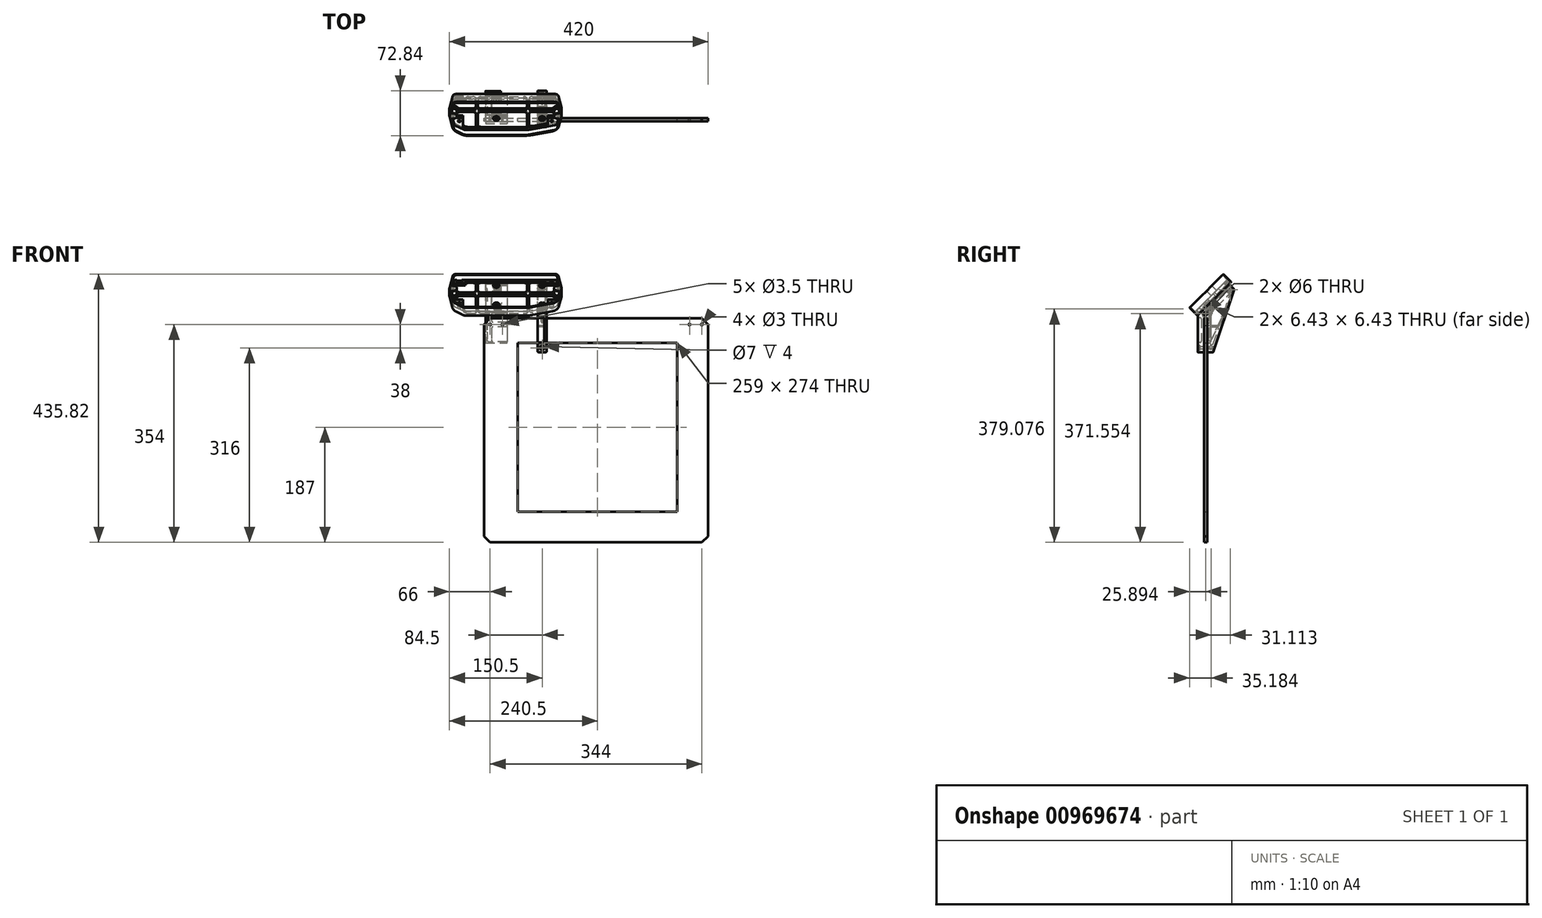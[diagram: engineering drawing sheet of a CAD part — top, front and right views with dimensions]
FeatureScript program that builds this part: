
annotation { "Feature Type Name" : "Feature", "Feature Type Description" : "" }
export const myFeature = defineFeature(function(context is Context, id is Id, definition is map)
    precondition{}
    {
        {
            var Q0;
            Q0=qCreatedBy(makeId("Front.planeOp"),FACE);
            var sketch = newSketch(context, id + "F0", { "sketchPlane" : qUnion([Q0])});
            skLineSegment(sketch, "E0.bottom", {"start": v(-182, 182) * mm, "end": v(182, 182) * mm});
            skLineSegment(sketch, "E0.top", {"start": v(-182, -182) * mm, "end": v(182, -182) * mm});
            skLineSegment(sketch, "E0.left", {"start": v(-182, 182) * mm, "end": v(-182, -182) * mm});
            skLineSegment(sketch, "E0.right", {"start": v(182, 182) * mm, "end": v(182, -182) * mm});
            skLineSegment(sketch, "E1", {"start": v(-182, 0) * mm, "end": v(0, 0) * mm, "construction": true});
            skLineSegment(sketch, "E2", {"start": v(0, 0) * mm, "end": v(0, 182) * mm, "construction": true});
            skLineSegment(sketch, "E3.bottom", {"start": v(-127, 142) * mm, "end": v(132, 142) * mm});
            skLineSegment(sketch, "E3.top", {"start": v(-127, -132) * mm, "end": v(132, -132) * mm});
            skLineSegment(sketch, "E3.left", {"start": v(-127, 142) * mm, "end": v(-127, -132) * mm});
            skLineSegment(sketch, "E3.right", {"start": v(132, 142) * mm, "end": v(132, -132) * mm});
            skCircle(sketch, "E4", {"center": v(172, 172) * mm, "radius": 1.5 * mm});
            skCircle(sketch, "E5", {"center": v(152, 172) * mm, "radius": 1.5 * mm});
            skCircle(sketch, "E6", {"center": v(-152, 172) * mm, "radius": 1.5 * mm});
            skCircle(sketch, "E7", {"center": v(-172, 172) * mm, "radius": 1.5 * mm});
            skSolve(sketch);
        }
        {
            var Q0;
            Q0=makeQuery(id+"F0.imprint","IMPRINT",FACE,{"disambiguationData":[TD([[makeQuery(id+"F0.imprint","IMPRINT",EDGE,{"derivedFrom":sQuery(id+"F0.wireOp",EDGE,"E0.bottom")}),-1.0]])]});
            extrude(context, id + "F1", {"entities" : qUnion([Q0]), "depth" : 5 * mm, "offsetDistance" : 25 * mm});
        }
        {
            var Q0;
            Q0=makeQuery(id+"F1.opExtrude","SWEPT_EDGE",EDGE,{"disambiguationData":[OSD([sQuery(id+"F0.wireOp",EDGE,"E0.bottom"),sQuery(id+"F0.wireOp",EDGE,"E0.left")])]});
            var Q1;
            Q1=makeQuery(id+"F1.opExtrude","SWEPT_EDGE",EDGE,{"disambiguationData":[OSD([sQuery(id+"F0.wireOp",EDGE,"E0.top"),sQuery(id+"F0.wireOp",EDGE,"E0.left")])]});
            var Q2;
            Q2=makeQuery(id+"F1.opExtrude","SWEPT_EDGE",EDGE,{"disambiguationData":[OSD([sQuery(id+"F0.wireOp",EDGE,"E0.top"),sQuery(id+"F0.wireOp",EDGE,"E0.right")])]});
            var Q3;
            Q3=makeQuery(id+"F1.opExtrude","SWEPT_EDGE",EDGE,{"disambiguationData":[OSD([sQuery(id+"F0.wireOp",EDGE,"E0.bottom"),sQuery(id+"F0.wireOp",EDGE,"E0.right")])]});
            chamfer(context, id + "F2", {"entities" : qUnion([Q0, Q1, Q2, Q3]), "width" : 10 * mm, "tangentPropagation" : true});
        }
        {
            var Q0;
            Q0=qCreatedBy(makeId("Right.planeOp"),FACE);
            cPlane(context, id + "F3", {"entities" : qUnion([Q0]), "cplaneType" : CPlaneType.OFFSET, "offset" : 80 * mm, "oppositeDirection" : true, "width" : 150 * mm, "height" : 150 * mm});
        }
        {
            var Q0;
            Q0=qCreatedBy(id+"F3.planeOp",FACE);
            var sketch = newSketch(context, id + "F4", { "sketchPlane" : qUnion([Q0])});
            skLineSegment(sketch, "E8", {"start": v(-5, 127) * mm, "end": v(-15, 127) * mm});
            skLineSegment(sketch, "E9", {"start": v(-15, 127) * mm, "end": v(-15, 187) * mm});
            skLineSegment(sketch, "E10", {"start": v(-15, 187) * mm, "end": v(35.91, 237.91) * mm});
            skLineSegment(sketch, "E11", {"start": v(35.91, 237.91) * mm, "end": v(44.4, 229.43) * mm});
            skLineSegment(sketch, "E12", {"start": v(44.4, 229.43) * mm, "end": v(10, 127) * mm});
            skLineSegment(sketch, "E13", {"start": v(10, 127) * mm, "end": v(0, 127) * mm});
            skLineSegment(sketch, "E14", {"start": v(0, 127) * mm, "end": v(0, 182) * mm});
            skLineSegment(sketch, "E15", {"start": v(0, 182) * mm, "end": v(-5, 182) * mm});
            skLineSegment(sketch, "E16", {"start": v(-5, 182) * mm, "end": v(-5, 127) * mm});
            skSolve(sketch);
        }
        {
            var Q0;
            Q0=makeQuery(id+"F4.imprint","IMPRINT",FACE,{"disambiguationData":[TD([[makeQuery(id+"F4.imprint","IMPRINT",EDGE,{"derivedFrom":sQuery(id+"F4.wireOp",EDGE,"E8")}),-1.0]])]});
            extrude(context, id + "F5", {"entities" : qUnion([Q0]), "oppositeDirection" : true, "depth" : 15 * mm, "offsetDistance" : 25 * mm});
        }
        {
            var Q0;
            Q0=makeQuery(id+"F5.opExtrude","SWEPT_FACE",FACE,{"disambiguationData":[OSD([sQuery(id+"F4.wireOp",EDGE,"E10")])]});
            var sketch = newSketch(context, id + "F6", { "sketchPlane" : qUnion([Q0])});
            skLineSegment(sketch, "E17.bottom", {"start": v(-232, 198.12) * mm, "end": v(-62, 198.12) * mm});
            skLineSegment(sketch, "E17.top", {"start": v(-232, 133.12) * mm, "end": v(-62, 133.12) * mm, "construction": true});
            skLineSegment(sketch, "E17.left", {"start": v(-232, 198.12) * mm, "end": v(-232, 133.12) * mm, "construction": true});
            skLineSegment(sketch, "E17.right", {"start": v(-62, 198.12) * mm, "end": v(-62, 133.12) * mm, "construction": true});
            skPoint(sketch, "E18.visualSharp", {"position": v(-232, 198.12) * mm});
            skPoint(sketch, "E19.visualSharp", {"position": v(-62, 133.12) * mm});
            skPoint(sketch, "E20.visualSharp", {"position": v(-232, 133.12) * mm});
            skLineSegment(sketch, "E21", {"start": v(-232, 133.12) * mm, "end": v(-214, 120.62) * mm});
            skLineSegment(sketch, "E22", {"start": v(-214, 120.62) * mm, "end": v(-110, 120.62) * mm});
            skLineSegment(sketch, "E23", {"start": v(-110, 120.62) * mm, "end": v(-62, 133.12) * mm});
            skLineSegment(sketch, "E24", {"start": v(-232, 133.12) * mm, "end": v(-237.9, 164.51) * mm});
            skLineSegment(sketch, "E25", {"start": v(-237.9, 166.73) * mm, "end": v(-232, 198.12) * mm});
            skLineSegment(sketch, "E26", {"start": v(-62, 198.12) * mm, "end": v(-56.1, 166.73) * mm});
            skLineSegment(sketch, "E27", {"start": v(-56.1, 164.51) * mm, "end": v(-62, 133.12) * mm});
            skPoint(sketch, "E28.visualSharp", {"position": v(-238.1, 165.62) * mm});
            skArc(sketch, "E28.filletArc", {"start": v(-237.9, 166.73) * mm, "mid": v(-238, 165.62) * mm, "end": v(-237.9, 164.51) * mm});
            skPoint(sketch, "E29.visualSharp", {"position": v(-55.9, 165.62) * mm});
            skArc(sketch, "E29.filletArc", {"start": v(-56.1, 164.51) * mm, "mid": v(-56, 165.62) * mm, "end": v(-56.1, 166.73) * mm});
            skLineSegment(sketch, "E30", {"start": v(-147, 198.12) * mm, "end": v(-147, 134.38) * mm, "construction": true});
            skSolve(sketch);
        }
        {
            var Q0;
            Q0 = qSketchRegion(id + "F6", true);
            extrude(context, id + "F7", {"entities" : qUnion([Q0]), "depth" : 18 * mm, "offsetDistance" : 25 * mm});
        }
        {
            var Q0;
            Q0=makeQuery(id+"F7.opExtrude","SWEPT_EDGE",EDGE,{"disambiguationData":[OSD([sQuery(id+"F6.wireOp",EDGE,"E21"),sQuery(id+"F6.wireOp",EDGE,"E24")])]});
            var Q1;
            Q1=makeQuery(id+"F7.opExtrude","SWEPT_EDGE",EDGE,{"disambiguationData":[OSD([sQuery(id+"F6.wireOp",EDGE,"E21"),sQuery(id+"F6.wireOp",EDGE,"E22")])]});
            var Q2;
            Q2=makeQuery(id+"F7.opExtrude","SWEPT_EDGE",EDGE,{"disambiguationData":[OSD([sQuery(id+"F6.wireOp",EDGE,"E23"),sQuery(id+"F6.wireOp",EDGE,"E27")])]});
            fillet(context, id + "F8", {"entities" : qUnion([Q0, Q1, Q2]), "radius" : 15 * mm, "tangentPropagation" : true, "allowEdgeOverflow" : false});
        }
        {
            var Q0;
            Q0=makeQuery(id+"F7.opExtrude","SWEPT_EDGE",EDGE,{"disambiguationData":[OSD([sQuery(id+"F6.wireOp",EDGE,"E22"),sQuery(id+"F6.wireOp",EDGE,"E23")])]});
            fillet(context, id + "F9", {"entities" : qUnion([Q0]), "radius" : 60 * mm, "tangentPropagation" : true, "allowEdgeOverflow" : false});
        }
        {
            var Q0;
            Q0=makeQuery(id+"F7.opExtrude","SWEPT_EDGE",EDGE,{"disambiguationData":[OSD([sQuery(id+"F6.wireOp",EDGE,"E17.bottom"),sQuery(id+"F6.wireOp",EDGE,"E25")])]});
            var Q1;
            Q1=makeQuery(id+"F7.opExtrude","SWEPT_EDGE",EDGE,{"disambiguationData":[OSD([sQuery(id+"F6.wireOp",EDGE,"E17.bottom"),sQuery(id+"F6.wireOp",EDGE,"E26")])]});
            fillet(context, id + "F10", {"entities" : qUnion([Q0, Q1]), "radius" : 5 * mm, "tangentPropagation" : true, "allowEdgeOverflow" : false});
        }
        {
            var Q0;
            Q0=makeQuery(id+"F5.opExtrude","SWEPT_FACE",FACE,{"disambiguationData":[OSD([sQuery(id+"F4.wireOp",EDGE,"E9")])]});
            var sketch = newSketch(context, id + "F11", { "sketchPlane" : qUnion([Q0])});
            skPoint(sketch, "E31", {"position": v(-87.5, 134) * mm});
            skPoint(sketch, "E31.positionSnap0", {"position": v(-87.5, 127) * mm});
            skSolve(sketch);
        }
        {
            var Q0;
            Q0=sQuery(id+"F11.wireOp",VERTEX,"E31");
            var Q1;
            Q1=makeQuery(id+"F5.opExtrude","SWEPT_BODY",BODY,{"disambiguationData":[OSD([sQuery(id+"F4.wireOp",EDGE,"E8"),sQuery(id+"F4.wireOp",EDGE,"E9"),sQuery(id+"F4.wireOp",EDGE,"E10"),sQuery(id+"F4.wireOp",EDGE,"E11"),sQuery(id+"F4.wireOp",EDGE,"E12"),sQuery(id+"F4.wireOp",EDGE,"E13"),sQuery(id+"F4.wireOp",EDGE,"E14"),sQuery(id+"F4.wireOp",EDGE,"E15"),sQuery(id+"F4.wireOp",EDGE,"E16")])]});
            hole(context, id + "F12", {"style" : HoleStyle.C_BORE, "endStyle" : HoleEndStyle.THROUGH, "holeDiameter" : 3.5 * mm, "cBoreDiameter" : 7 * mm, "cBoreDepth" : 4 * mm, "majorDiameter" : 5 * mm, "isTappedThrough" : true, "tappedDepth" : 12 * mm, "tapClearance" : 3, "locations" : qUnion([Q0]), "scope" : qUnion([Q1])});
        }
        {
            var Q0;
            Q0=makeQuery(id+"F7.opExtrude","CAP_FACE",FACE,{"disambiguationData":[OSD([sQuery(id+"F6.wireOp",EDGE,"E17.bottom"),sQuery(id+"F6.wireOp",EDGE,"E17.top"),sQuery(id+"F6.wireOp",EDGE,"E17.left"),sQuery(id+"F6.wireOp",EDGE,"E17.right")])],"isStart":true});
            var sketch = newSketch(context, id + "F13", { "sketchPlane" : qUnion([Q0])});
            skLineSegment(sketch, "E32.bottom", {"start": v(67, 196.17) * mm, "end": v(77, 196.17) * mm});
            skLineSegment(sketch, "E32.top", {"start": v(67, 190.07) * mm, "end": v(77, 190.07) * mm});
            skLineSegment(sketch, "E32.left", {"start": v(67, 196.17) * mm, "end": v(67, 190.07) * mm, "construction": true});
            skLineSegment(sketch, "E32.right", {"start": v(77, 196.17) * mm, "end": v(77, 190.07) * mm, "construction": true});
            skLineSegment(sketch, "E33.bottom", {"start": v(68.95, 138.12) * mm, "end": v(75.05, 138.12) * mm, "construction": true});
            skLineSegment(sketch, "E33.top", {"start": v(68.95, 148.12) * mm, "end": v(75.05, 148.12) * mm, "construction": true});
            skLineSegment(sketch, "E33.right", {"start": v(75.05, 138.12) * mm, "end": v(75.05, 148.12) * mm});
            skLineSegment(sketch, "E34.bottom", {"start": v(218.95, 148.12) * mm, "end": v(225.05, 148.12) * mm, "construction": true});
            skLineSegment(sketch, "E34.top", {"start": v(218.95, 138.12) * mm, "end": v(225.05, 138.12) * mm, "construction": true});
            skLineSegment(sketch, "E34.left", {"start": v(218.95, 148.12) * mm, "end": v(218.95, 138.12) * mm});
            skLineSegment(sketch, "E34.right", {"start": v(225.05, 148.12) * mm, "end": v(225.05, 138.12) * mm});
            skPoint(sketch, "E35.firstSnap0", {"position": v(72, 196.17) * mm});
            skLineSegment(sketch, "E35.bottom", {"start": v(72, 193.12) * mm, "end": v(222, 193.12) * mm, "construction": true});
            skLineSegment(sketch, "E35.top", {"start": v(72, 143.12) * mm, "end": v(222, 143.12) * mm, "construction": true});
            skLineSegment(sketch, "E35.left", {"start": v(72, 193.12) * mm, "end": v(72, 143.12) * mm, "construction": true});
            skLineSegment(sketch, "E35.right", {"start": v(222, 193.12) * mm, "end": v(222, 143.12) * mm, "construction": true});
            skLineSegment(sketch, "E36.bottom", {"start": v(227, 196.17) * mm, "end": v(217, 196.17) * mm});
            skLineSegment(sketch, "E36.top", {"start": v(227, 190.07) * mm, "end": v(217, 190.07) * mm});
            skLineSegment(sketch, "E36.left", {"start": v(227, 196.17) * mm, "end": v(227, 190.07) * mm, "construction": true});
            skLineSegment(sketch, "E36.right", {"start": v(217, 196.17) * mm, "end": v(217, 190.07) * mm, "construction": true});
            skLineSegment(sketch, "E37", {"start": v(68.95, 138.12) * mm, "end": v(68.95, 148.12) * mm});
            skLineSegment(sketch, "E38", {"start": v(67, 196.17) * mm, "end": v(65.24, 193.12) * mm});
            skLineSegment(sketch, "E39", {"start": v(65.24, 193.12) * mm, "end": v(67, 190.07) * mm});
            skLineSegment(sketch, "E40", {"start": v(77, 190.07) * mm, "end": v(78.76, 193.12) * mm});
            skLineSegment(sketch, "E41", {"start": v(78.76, 193.12) * mm, "end": v(77, 196.17) * mm});
            skLineSegment(sketch, "E42", {"start": v(68.95, 148.12) * mm, "end": v(72, 149.88) * mm});
            skLineSegment(sketch, "E43", {"start": v(72, 149.88) * mm, "end": v(75.05, 148.12) * mm});
            skLineSegment(sketch, "E44", {"start": v(72, 136.36) * mm, "end": v(75.05, 138.12) * mm});
            skLineSegment(sketch, "E45", {"start": v(68.95, 138.12) * mm, "end": v(72, 136.36) * mm});
            skLineSegment(sketch, "E46", {"start": v(218.95, 148.12) * mm, "end": v(222, 149.88) * mm});
            skLineSegment(sketch, "E47", {"start": v(222, 149.88) * mm, "end": v(225.05, 148.12) * mm});
            skLineSegment(sketch, "E48", {"start": v(225.05, 138.12) * mm, "end": v(222, 136.36) * mm});
            skLineSegment(sketch, "E49", {"start": v(222, 136.36) * mm, "end": v(218.95, 138.12) * mm});
            skLineSegment(sketch, "E50", {"start": v(227, 196.17) * mm, "end": v(228.76, 193.12) * mm});
            skLineSegment(sketch, "E51", {"start": v(228.76, 193.12) * mm, "end": v(227, 190.07) * mm});
            skLineSegment(sketch, "E52", {"start": v(217, 190.07) * mm, "end": v(215.24, 193.12) * mm});
            skLineSegment(sketch, "E53", {"start": v(215.24, 193.12) * mm, "end": v(217, 196.17) * mm});
            skSolve(sketch);
        }
        {
            var Q0;
            Q0 = qSketchRegion(id + "F13", true);
            extrude(context, id + "F14", {"entities" : qUnion([Q0]), "operationType" : NewBodyOperationType.REMOVE, "oppositeDirection" : true, "depth" : 4 * mm, "offsetDistance" : 25 * mm});
        }
        {
            var Q0;
            Q0=sQuery(id+"F13.wireOp",VERTEX,"E35.bottom.start");
            var Q1;
            Q1=sQuery(id+"F13.wireOp",VERTEX,"E35.bottom.end");
            var Q2;
            Q2=sQuery(id+"F13.wireOp",VERTEX,"E35.top.end");
            var Q3;
            Q3=sQuery(id+"F13.wireOp",VERTEX,"E35.top.start");
            var Q4;
            Q4=makeQuery(id+"F7.opExtrude","SWEPT_BODY",BODY,{"disambiguationData":[OSD([sQuery(id+"F6.wireOp",EDGE,"E17.bottom"),sQuery(id+"F6.wireOp",EDGE,"E17.top"),sQuery(id+"F6.wireOp",EDGE,"E17.left"),sQuery(id+"F6.wireOp",EDGE,"E17.right")])]});
            hole(context, id + "F15", {"style" : HoleStyle.SIMPLE, "endStyle" : HoleEndStyle.THROUGH, "standardTappedOrClearance" : lookupTablePath({ "fit" : "Normal", "standard" : "ISO", "size" : "M3", "type" : "Clearance" }), "standardBlindInLast" : lookupTablePath({ "fit" : "Normal", "standard" : "ISO", "engagement" : "75%", "pitch" : "0.5 mm", "size" : "M3", "type" : "Clearance & tapped" }), "holeDiameter" : 3.4 * mm, "majorDiameter" : 5 * mm, "isTappedThrough" : true, "tappedDepth" : 12 * mm, "tapClearance" : 3, "locations" : qUnion([Q0, Q1, Q2, Q3]), "scope" : qUnion([Q4])});
        }
        {
            var Q0;
            Q0=makeQuery(id+"F7.opExtrude","CAP_FACE",FACE,{"disambiguationData":[OSD([sQuery(id+"F6.wireOp",EDGE,"E17.bottom"),sQuery(id+"F6.wireOp",EDGE,"E21"),sQuery(id+"F6.wireOp",EDGE,"E22"),sQuery(id+"F6.wireOp",EDGE,"E23"),sQuery(id+"F6.wireOp",EDGE,"E24"),sQuery(id+"F6.wireOp",EDGE,"E25"),sQuery(id+"F6.wireOp",EDGE,"E26"),sQuery(id+"F6.wireOp",EDGE,"E27"),sQuery(id+"F6.wireOp",EDGE,"E28.filletArc"),sQuery(id+"F6.wireOp",EDGE,"E29.filletArc")])],"isStart":false});
            var sketch = newSketch(context, id + "F16", { "sketchPlane" : qUnion([Q0])});
            skArc(sketch, "E54", {"start": v(-232.4, 171.6) * mm, "mid": v(-226, 165.62) * mm, "end": v(-232.4, 159.64) * mm});
            skLineSegment(sketch, "E55", {"start": v(-234.5, 173.97) * mm, "end": v(-231.1, 192.05) * mm});
            skLineSegment(sketch, "E56", {"start": v(-226.2, 196.12) * mm, "end": v(-67.8, 196.12) * mm});
            skLineSegment(sketch, "E57", {"start": v(-59.5, 157.27) * mm, "end": v(-63.15, 137.85) * mm});
            skLineSegment(sketch, "E58", {"start": v(-66.8, 133.94) * mm, "end": v(-109.64, 122.78) * mm});
            skLineSegment(sketch, "E59", {"start": v(-110.9, 122.62) * mm, "end": v(-211.8, 122.62) * mm});
            skLineSegment(sketch, "E60", {"start": v(-214.66, 123.52) * mm, "end": v(-228.5, 133.13) * mm});
            skLineSegment(sketch, "E61", {"start": v(-230.56, 136.31) * mm, "end": v(-234.5, 157.27) * mm});
            skArc(sketch, "E62", {"start": v(-61.6, 171.6) * mm, "mid": v(-68, 165.62) * mm, "end": v(-61.6, 159.64) * mm});
            skLineSegment(sketch, "E63", {"start": v(-62.9, 192.05) * mm, "end": v(-59.5, 173.97) * mm});
            skPoint(sketch, "E64.visualSharp", {"position": v(-235.1, 170.76) * mm});
            skArc(sketch, "E64.filletArc", {"start": v(-234.5, 173.97) * mm, "mid": v(-234.03, 172.28) * mm, "end": v(-232.4, 171.6) * mm});
            skPoint(sketch, "E65.visualSharp", {"position": v(-235.1, 160.49) * mm});
            skArc(sketch, "E65.filletArc", {"start": v(-232.4, 159.64) * mm, "mid": v(-234.03, 158.97) * mm, "end": v(-234.5, 157.27) * mm});
            skPoint(sketch, "E66.visualSharp", {"position": v(-58.9, 170.76) * mm});
            skArc(sketch, "E66.filletArc", {"start": v(-61.6, 171.6) * mm, "mid": v(-59.97, 172.28) * mm, "end": v(-59.5, 173.97) * mm});
            skPoint(sketch, "E67.visualSharp", {"position": v(-58.9, 160.49) * mm});
            skArc(sketch, "E67.filletArc", {"start": v(-59.5, 157.27) * mm, "mid": v(-59.97, 158.97) * mm, "end": v(-61.6, 159.64) * mm});
            skPoint(sketch, "E68.visualSharp", {"position": v(-63.66, 196.12) * mm});
            skArc(sketch, "E68.filletArc", {"start": v(-62.9, 192.05) * mm, "mid": v(-64.61, 194.97) * mm, "end": v(-67.8, 196.12) * mm});
            skPoint(sketch, "E69.visualSharp", {"position": v(-63.73, 134.74) * mm});
            skArc(sketch, "E69.filletArc", {"start": v(-66.8, 133.94) * mm, "mid": v(-64.4, 135.37) * mm, "end": v(-63.15, 137.85) * mm});
            skPoint(sketch, "E70.visualSharp", {"position": v(-110.26, 122.62) * mm});
            skArc(sketch, "E70.filletArc", {"start": v(-110.9, 122.62) * mm, "mid": v(-110.26, 122.66) * mm, "end": v(-109.64, 122.78) * mm});
            skPoint(sketch, "E71.visualSharp", {"position": v(-213.37, 122.62) * mm});
            skArc(sketch, "E71.filletArc", {"start": v(-214.66, 123.52) * mm, "mid": v(-213.3, 122.85) * mm, "end": v(-211.8, 122.62) * mm});
            skPoint(sketch, "E72.visualSharp", {"position": v(-230.19, 134.3) * mm});
            skArc(sketch, "E72.filletArc", {"start": v(-230.56, 136.31) * mm, "mid": v(-229.85, 134.52) * mm, "end": v(-228.5, 133.13) * mm});
            skPoint(sketch, "E73.visualSharp", {"position": v(-230.34, 196.12) * mm});
            skArc(sketch, "E73.filletArc", {"start": v(-226.2, 196.12) * mm, "mid": v(-229.39, 194.97) * mm, "end": v(-231.1, 192.05) * mm});
            skSolve(sketch);
        }
        {
            var Q0;
            Q0 = qSketchRegion(id + "F16", true);
            extrude(context, id + "F17", {"entities" : qUnion([Q0]), "operationType" : NewBodyOperationType.REMOVE, "oppositeDirection" : true, "depth" : 11 * mm, "offsetDistance" : 25 * mm});
        }
        {
            var Q0;
            Q0=qCreatedBy(id+"F3.planeOp",FACE);
            cPlane(context, id + "F18", {"entities" : qUnion([Q0]), "cplaneType" : CPlaneType.OFFSET, "offset" : (65 + 17) * mm, "oppositeDirection" : true, "width" : 150 * mm, "height" : 150 * mm});
        }
        {
            var Q0;
            Q0=qCreatedBy(id+"F18.planeOp",FACE);
            var sketch = newSketch(context, id + "F19", { "sketchPlane" : qUnion([Q0])});
            skLineSegment(sketch, "E74", {"start": v(35.91, 237.91) * mm, "end": v(-9, 193) * mm});
            skLineSegment(sketch, "E75", {"start": v(0, 182) * mm, "end": v(0, 142) * mm});
            skLineSegment(sketch, "E76", {"start": v(0, 142) * mm, "end": v(5, 142) * mm});
            skLineSegment(sketch, "E77", {"start": v(5, 142) * mm, "end": v(44.4, 229.43) * mm});
            skLineSegment(sketch, "E78", {"start": v(44.4, 229.43) * mm, "end": v(35.91, 237.91) * mm});
            skLineSegment(sketch, "E79", {"start": v(0, 182) * mm, "end": v(-5, 182) * mm});
            skLineSegment(sketch, "E80", {"start": v(-5, 182) * mm, "end": v(-9, 193) * mm});
            skSolve(sketch);
        }
        {
            var Q0;
            Q0=makeQuery(id+"F19.imprint","IMPRINT",FACE,{"disambiguationData":[TD([[makeQuery(id+"F19.imprint","IMPRINT",EDGE,{"derivedFrom":sQuery(id+"F19.wireOp",EDGE,"E74")}),1.0]])]});
            extrude(context, id + "F20", {"entities" : qUnion([Q0]), "endBound" : BoundingType.SYMMETRIC, "oppositeDirection" : true, "depth" : 35 * mm, "offsetDistance" : 25 * mm});
        }
        {
            var Q0;
            Q0=makeQuery(id+"F17.boolean.opBoolean","COPY",FACE,{"derivedFrom":makeQuery(id+"F17.opExtrude","CAP_FACE",FACE,{"disambiguationData":[OSD([sQuery(id+"F16.wireOp",EDGE,"E54"),sQuery(id+"F16.wireOp",EDGE,"E55"),sQuery(id+"F16.wireOp",EDGE,"E56"),sQuery(id+"F16.wireOp",EDGE,"E57"),sQuery(id+"F16.wireOp",EDGE,"E58"),sQuery(id+"F16.wireOp",EDGE,"E59"),sQuery(id+"F16.wireOp",EDGE,"E60"),sQuery(id+"F16.wireOp",EDGE,"E61"),sQuery(id+"F16.wireOp",EDGE,"E62"),sQuery(id+"F16.wireOp",EDGE,"E63"),sQuery(id+"F16.wireOp",EDGE,"E64.filletArc"),sQuery(id+"F16.wireOp",EDGE,"E65.filletArc"),sQuery(id+"F16.wireOp",EDGE,"E66.filletArc"),sQuery(id+"F16.wireOp",EDGE,"E67.filletArc"),sQuery(id+"F16.wireOp",EDGE,"E68.filletArc"),sQuery(id+"F16.wireOp",EDGE,"E69.filletArc"),sQuery(id+"F16.wireOp",EDGE,"E70.filletArc"),sQuery(id+"F16.wireOp",EDGE,"E71.filletArc"),sQuery(id+"F16.wireOp",EDGE,"E72.filletArc"),sQuery(id+"F16.wireOp",EDGE,"E73.filletArc")])],"isStart":false})});
            var sketch = newSketch(context, id + "F21", { "sketchPlane" : qUnion([Q0])});
            skLineSegment(sketch, "E81.bottom", {"start": v(-162, 188.12) * mm, "end": v(-87.5, 188.12) * mm, "construction": true});
            skLineSegment(sketch, "E81.top", {"start": v(-162, 144.12) * mm, "end": v(-87.5, 144.12) * mm, "construction": true});
            skLineSegment(sketch, "E81.left", {"start": v(-162, 188.12) * mm, "end": v(-162, 144.12) * mm, "construction": true});
            skLineSegment(sketch, "E81.right", {"start": v(-87.5, 188.12) * mm, "end": v(-87.5, 144.12) * mm, "construction": true});
            skCircle(sketch, "E82", {"center": v(-162, 188.12) * mm, "radius": 4 * mm});
            skCircle(sketch, "E83", {"center": v(-87.5, 188.12) * mm, "radius": 4 * mm});
            skCircle(sketch, "E84", {"center": v(-87.5, 144.12) * mm, "radius": 4 * mm});
            skCircle(sketch, "E85", {"center": v(-162, 144.12) * mm, "radius": 4 * mm});
            skCircle(sketch, "E86", {"center": v(-162, 188.12) * mm, "radius": 5 * mm});
            skCircle(sketch, "E87", {"center": v(-162, 144.12) * mm, "radius": 5 * mm});
            skCircle(sketch, "E88", {"center": v(-87.5, 144.12) * mm, "radius": 5 * mm});
            skCircle(sketch, "E89", {"center": v(-87.5, 188.12) * mm, "radius": 5 * mm});
            skSolve(sketch);
        }
        {
            var Q0;
            Q0=makeQuery(id+"F21.imprint","IMPRINT",FACE,{"disambiguationData":[TD([[makeQuery(id+"F21.imprint","IMPRINT",EDGE,{"derivedFrom":sQuery(id+"F21.wireOp",EDGE,"E83")}),-1.0]])]});
            var Q1;
            Q1=makeQuery(id+"F21.imprint","IMPRINT",FACE,{"disambiguationData":[TD([[makeQuery(id+"F21.imprint","IMPRINT",EDGE,{"derivedFrom":sQuery(id+"F21.wireOp",EDGE,"E83")}),1.0]])]});
            var Q2;
            Q2=makeQuery(id+"F21.imprint","IMPRINT",FACE,{"disambiguationData":[TD([[makeQuery(id+"F21.imprint","IMPRINT",EDGE,{"derivedFrom":sQuery(id+"F21.wireOp",EDGE,"E84")}),-1.0]])]});
            var Q3;
            Q3=makeQuery(id+"F21.imprint","IMPRINT",FACE,{"disambiguationData":[TD([[makeQuery(id+"F21.imprint","IMPRINT",EDGE,{"derivedFrom":sQuery(id+"F21.wireOp",EDGE,"E84")}),1.0]])]});
            var Q4;
            Q4=makeQuery(id+"F21.imprint","IMPRINT",FACE,{"disambiguationData":[TD([[makeQuery(id+"F21.imprint","IMPRINT",EDGE,{"derivedFrom":sQuery(id+"F21.wireOp",EDGE,"E85")}),-1.0]])]});
            var Q5;
            Q5=makeQuery(id+"F21.imprint","IMPRINT",FACE,{"disambiguationData":[TD([[makeQuery(id+"F21.imprint","IMPRINT",EDGE,{"derivedFrom":sQuery(id+"F21.wireOp",EDGE,"E85")}),1.0]])]});
            var Q6;
            Q6=makeQuery(id+"F21.imprint","IMPRINT",FACE,{"disambiguationData":[TD([[makeQuery(id+"F21.imprint","IMPRINT",EDGE,{"derivedFrom":sQuery(id+"F21.wireOp",EDGE,"E82")}),-1.0]])]});
            var Q7;
            Q7=makeQuery(id+"F21.imprint","IMPRINT",FACE,{"disambiguationData":[TD([[makeQuery(id+"F21.imprint","IMPRINT",EDGE,{"derivedFrom":sQuery(id+"F21.wireOp",EDGE,"E82")}),1.0]])]});
            var Q8;
            Q8=makeQuery(id+"F7.opExtrude","CAP_FACE",FACE,{"disambiguationData":[OSD([sQuery(id+"F6.wireOp",EDGE,"E17.bottom"),sQuery(id+"F6.wireOp",EDGE,"E21"),sQuery(id+"F6.wireOp",EDGE,"E22"),sQuery(id+"F6.wireOp",EDGE,"E23"),sQuery(id+"F6.wireOp",EDGE,"E24"),sQuery(id+"F6.wireOp",EDGE,"E25"),sQuery(id+"F6.wireOp",EDGE,"E26"),sQuery(id+"F6.wireOp",EDGE,"E27"),sQuery(id+"F6.wireOp",EDGE,"E28.filletArc"),sQuery(id+"F6.wireOp",EDGE,"E29.filletArc")])],"isStart":true});
            extrude(context, id + "F22", {"entities" : qUnion([Q0, Q1, Q2, Q3, Q4, Q5, Q6, Q7]), "operationType" : NewBodyOperationType.ADD, "endBound" : BoundingType.UP_TO_SURFACE, "oppositeDirection" : true, "depth" : 25 * mm, "endBoundEntityFace" : qUnion([Q8]), "hasOffset" : true, "offsetDistance" : 2.5 * mm, "offsetOppositeDirection" : true});
        }
        {
            var Q0;
            Q0=makeQuery(id+"F21.imprint","IMPRINT",FACE,{"disambiguationData":[TD([[makeQuery(id+"F21.imprint","IMPRINT",EDGE,{"derivedFrom":sQuery(id+"F21.wireOp",EDGE,"E82")}),-1.0]])]});
            var Q1;
            Q1=makeQuery(id+"F21.imprint","IMPRINT",FACE,{"disambiguationData":[TD([[makeQuery(id+"F21.imprint","IMPRINT",EDGE,{"derivedFrom":sQuery(id+"F21.wireOp",EDGE,"E82")}),1.0]])]});
            var Q2;
            Q2=makeQuery(id+"F21.imprint","IMPRINT",FACE,{"disambiguationData":[TD([[makeQuery(id+"F21.imprint","IMPRINT",EDGE,{"derivedFrom":sQuery(id+"F21.wireOp",EDGE,"E83")}),-1.0]])]});
            var Q3;
            Q3=makeQuery(id+"F21.imprint","IMPRINT",FACE,{"disambiguationData":[TD([[makeQuery(id+"F21.imprint","IMPRINT",EDGE,{"derivedFrom":sQuery(id+"F21.wireOp",EDGE,"E83")}),1.0]])]});
            var Q4;
            Q4=makeQuery(id+"F21.imprint","IMPRINT",FACE,{"disambiguationData":[TD([[makeQuery(id+"F21.imprint","IMPRINT",EDGE,{"derivedFrom":sQuery(id+"F21.wireOp",EDGE,"E84")}),-1.0]])]});
            var Q5;
            Q5=makeQuery(id+"F21.imprint","IMPRINT",FACE,{"disambiguationData":[TD([[makeQuery(id+"F21.imprint","IMPRINT",EDGE,{"derivedFrom":sQuery(id+"F21.wireOp",EDGE,"E84")}),1.0]])]});
            var Q6;
            Q6=makeQuery(id+"F21.imprint","IMPRINT",FACE,{"disambiguationData":[TD([[makeQuery(id+"F21.imprint","IMPRINT",EDGE,{"derivedFrom":sQuery(id+"F21.wireOp",EDGE,"E85")}),-1.0]])]});
            var Q7;
            Q7=makeQuery(id+"F21.imprint","IMPRINT",FACE,{"disambiguationData":[TD([[makeQuery(id+"F21.imprint","IMPRINT",EDGE,{"derivedFrom":sQuery(id+"F21.wireOp",EDGE,"E85")}),1.0]])]});
            extrude(context, id + "F23", {"entities" : qUnion([Q0, Q1, Q2, Q3, Q4, Q5, Q6, Q7]), "operationType" : NewBodyOperationType.REMOVE, "oppositeDirection" : true, "depth" : 10 * mm, "offsetDistance" : 25 * mm});
        }
        {
            var Q0;
            Q0=sQuery(id+"F21.wireOp",VERTEX,"E81.bottom.start");
            var Q1;
            Q1=sQuery(id+"F21.wireOp",VERTEX,"E81.bottom.end");
            var Q2;
            Q2=sQuery(id+"F21.wireOp",VERTEX,"E81.top.end");
            var Q3;
            Q3=sQuery(id+"F21.wireOp",VERTEX,"E81.top.start");
            var Q4;
            Q4=makeQuery(id+"F7.opExtrude","SWEPT_BODY",BODY,{"disambiguationData":[OSD([sQuery(id+"F6.wireOp",EDGE,"E17.bottom"),sQuery(id+"F6.wireOp",EDGE,"E21"),sQuery(id+"F6.wireOp",EDGE,"E22"),sQuery(id+"F6.wireOp",EDGE,"E23"),sQuery(id+"F6.wireOp",EDGE,"E24"),sQuery(id+"F6.wireOp",EDGE,"E25"),sQuery(id+"F6.wireOp",EDGE,"E26"),sQuery(id+"F6.wireOp",EDGE,"E27"),sQuery(id+"F6.wireOp",EDGE,"E28.filletArc"),sQuery(id+"F6.wireOp",EDGE,"E29.filletArc")])]});
            var Q5;
            Q5=makeQuery(id+"F5.opExtrude","SWEPT_BODY",BODY,{"disambiguationData":[OSD([sQuery(id+"F4.wireOp",EDGE,"E8"),sQuery(id+"F4.wireOp",EDGE,"E9"),sQuery(id+"F4.wireOp",EDGE,"E10"),sQuery(id+"F4.wireOp",EDGE,"E11"),sQuery(id+"F4.wireOp",EDGE,"E12"),sQuery(id+"F4.wireOp",EDGE,"E13"),sQuery(id+"F4.wireOp",EDGE,"E14"),sQuery(id+"F4.wireOp",EDGE,"E15"),sQuery(id+"F4.wireOp",EDGE,"E16")])]});
            var Q6;
            Q6=makeQuery(id+"F20.opExtrude","SWEPT_BODY",BODY,{"disambiguationData":[OSD([sQuery(id+"F19.wireOp",EDGE,"E74"),sQuery(id+"F19.wireOp",EDGE,"E75"),sQuery(id+"F19.wireOp",EDGE,"E76"),sQuery(id+"F19.wireOp",EDGE,"E77"),sQuery(id+"F19.wireOp",EDGE,"E78")])]});
            hole(context, id + "F24", {"style" : HoleStyle.C_BORE, "endStyle" : HoleEndStyle.THROUGH, "holeDiameter" : 3.4 * mm, "cBoreDiameter" : 6.5 * mm, "cBoreDepth" : 4 * mm, "majorDiameter" : 5 * mm, "isTappedThrough" : true, "tappedDepth" : 12 * mm, "tapClearance" : 3, "locations" : qUnion([Q0, Q1, Q2, Q3]), "scope" : qUnion([Q4, Q5, Q6])});
        }
        {
            var Q0;
            Q0=makeQuery(id+"F17.boolean.opBoolean","COPY",FACE,{"derivedFrom":makeQuery(id+"F17.opExtrude","CAP_FACE",FACE,{"disambiguationData":[OSD([sQuery(id+"F16.wireOp",EDGE,"E54"),sQuery(id+"F16.wireOp",EDGE,"E55"),sQuery(id+"F16.wireOp",EDGE,"E56"),sQuery(id+"F16.wireOp",EDGE,"E57"),sQuery(id+"F16.wireOp",EDGE,"E58"),sQuery(id+"F16.wireOp",EDGE,"E59"),sQuery(id+"F16.wireOp",EDGE,"E60"),sQuery(id+"F16.wireOp",EDGE,"E61"),sQuery(id+"F16.wireOp",EDGE,"E62"),sQuery(id+"F16.wireOp",EDGE,"E63"),sQuery(id+"F16.wireOp",EDGE,"E64.filletArc"),sQuery(id+"F16.wireOp",EDGE,"E65.filletArc"),sQuery(id+"F16.wireOp",EDGE,"E66.filletArc"),sQuery(id+"F16.wireOp",EDGE,"E67.filletArc"),sQuery(id+"F16.wireOp",EDGE,"E68.filletArc"),sQuery(id+"F16.wireOp",EDGE,"E69.filletArc"),sQuery(id+"F16.wireOp",EDGE,"E70.filletArc"),sQuery(id+"F16.wireOp",EDGE,"E71.filletArc"),sQuery(id+"F16.wireOp",EDGE,"E72.filletArc"),sQuery(id+"F16.wireOp",EDGE,"E73.filletArc")])],"isStart":false})});
            var sketch = newSketch(context, id + "F25", { "sketchPlane" : qUnion([Q0])});
            skLineSegment(sketch, "E90", {"start": v(-212.3, 194.12) * mm, "end": v(-112, 194.12) * mm});
            skLineSegment(sketch, "E91", {"start": v(-64.2, 188.12) * mm, "end": v(-61.88, 175.82) * mm});
            skLineSegment(sketch, "E92", {"start": v(-229.8, 188.12) * mm, "end": v(-232.12, 175.82) * mm});
            skArc(sketch, "E93", {"start": v(-230.52, 173.48) * mm, "mid": v(-226.35, 171.29) * mm, "end": v(-224.14, 167.12) * mm});
            skArc(sketch, "E94", {"start": v(-230.52, 173.48) * mm, "mid": v(-231.8, 174.32) * mm, "end": v(-232.12, 175.82) * mm});
            skPoint(sketch, "E95.startSnap0", {"position": v(-224.14, 164.12) * mm});
            skLineSegment(sketch, "E96", {"start": v(-231.62, 152.75) * mm, "end": v(-232.12, 155.43) * mm});
            skLineSegment(sketch, "E97", {"start": v(-209.1, 124.62) * mm, "end": v(-111.15, 124.62) * mm});
            skArc(sketch, "E98", {"start": v(-63.48, 173.48) * mm, "mid": v(-70, 165.62) * mm, "end": v(-63.48, 157.76) * mm});
            skPoint(sketch, "E98.centerSnap0", {"position": v(-68, 165.62) * mm});
            skPoint(sketch, "E99.visualSharp", {"position": v(-232.54, 157.64) * mm});
            skArc(sketch, "E99.filletArc", {"start": v(-230.52, 157.76) * mm, "mid": v(-231.8, 156.92) * mm, "end": v(-232.12, 155.43) * mm});
            skArc(sketch, "E100.filletArc", {"start": v(-231.62, 152.75) * mm, "mid": v(-230.93, 151.58) * mm, "end": v(-229.65, 151.12) * mm});
            skArc(sketch, "E101", {"start": v(-63.48, 173.48) * mm, "mid": v(-62.2, 174.32) * mm, "end": v(-61.88, 175.82) * mm});
            skLineSegment(sketch, "E102", {"start": v(-229.8, 188.12) * mm, "end": v(-212.3, 188.12) * mm});
            skLineSegment(sketch, "E103", {"start": v(-212.3, 188.12) * mm, "end": v(-212.3, 194.12) * mm});
            skLineSegment(sketch, "E104", {"start": v(-81.7, 194.12) * mm, "end": v(-81.7, 188.12) * mm});
            skLineSegment(sketch, "E105", {"start": v(-81.7, 188.12) * mm, "end": v(-64.2, 188.12) * mm});
            skLineSegment(sketch, "E106", {"start": v(-216, 130.94) * mm, "end": v(-216, 151.12) * mm});
            skLineSegment(sketch, "E107", {"start": v(-216, 151.12) * mm, "end": v(-229.65, 151.12) * mm});
            skPoint(sketch, "E108", {"position": v(-222, 143.12) * mm});
            skLineSegment(sketch, "E109", {"start": v(-147, 194.12) * mm, "end": v(-147, 153.63) * mm, "construction": true});
            skLineSegment(sketch, "E110.MirrorCS", {"start": v(-78, 136.95) * mm, "end": v(-78, 151.12) * mm});
            skLineSegment(sketch, "E111.MirrorCS", {"start": v(-78, 151.12) * mm, "end": v(-64.35, 151.12) * mm});
            skLineSegment(sketch, "E112.MirrorCS", {"start": v(-62.38, 152.75) * mm, "end": v(-61.88, 155.43) * mm});
            skArc(sketch, "E113.MirrorCS", {"start": v(-62.38, 152.75) * mm, "mid": v(-63.07, 151.58) * mm, "end": v(-64.35, 151.12) * mm});
            skArc(sketch, "E114.MirrorCS", {"start": v(-63.48, 157.76) * mm, "mid": v(-62.2, 156.92) * mm, "end": v(-61.88, 155.43) * mm});
            skLineSegment(sketch, "E115", {"start": v(-213.85, 126.83) * mm, "end": v(-211.96, 125.52) * mm});
            skLineSegment(sketch, "E116", {"start": v(-81.74, 132.12) * mm, "end": v(-109.9, 124.78) * mm});
            skPoint(sketch, "E117", {"position": v(-221.58, 128.32) * mm});
            skPoint(sketch, "E118.visualSharp", {"position": v(-216, 128.32) * mm});
            skArc(sketch, "E118.filletArc", {"start": v(-216, 130.94) * mm, "mid": v(-215.43, 128.62) * mm, "end": v(-213.85, 126.83) * mm});
            skPoint(sketch, "E119.visualSharp", {"position": v(-210.67, 124.62) * mm});
            skArc(sketch, "E119.filletArc", {"start": v(-211.96, 125.52) * mm, "mid": v(-210.6, 124.85) * mm, "end": v(-209.1, 124.62) * mm});
            skPoint(sketch, "E120.visualSharp", {"position": v(-110.51, 124.62) * mm});
            skArc(sketch, "E120.filletArc", {"start": v(-111.15, 124.62) * mm, "mid": v(-110.52, 124.66) * mm, "end": v(-109.9, 124.78) * mm});
            skPoint(sketch, "E121.visualSharp", {"position": v(-78, 133.09) * mm});
            skArc(sketch, "E121.filletArc", {"start": v(-81.74, 132.12) * mm, "mid": v(-79.04, 133.9) * mm, "end": v(-78, 136.95) * mm});
            skLineSegment(sketch, "E122", {"start": v(-195, 194.12) * mm, "end": v(-195, 167.12) * mm});
            skLineSegment(sketch, "E123", {"start": v(-192, 194.12) * mm, "end": v(-192, 167.12) * mm});
            skLineSegment(sketch, "E124", {"start": v(-112, 194.12) * mm, "end": v(-112, 167.12) * mm});
            skLineSegment(sketch, "E125", {"start": v(-109, 124.62) * mm, "end": v(-109, 164.12) * mm});
            skLineSegment(sketch, "E126", {"start": v(-69.86, 167.12) * mm, "end": v(-109, 167.12) * mm});
            skLineSegment(sketch, "E127", {"start": v(-224.14, 164.12) * mm, "end": v(-195, 164.12) * mm});
            skLineSegment(sketch, "E128.trimOffspring", {"start": v(-195, 167.12) * mm, "end": v(-224.14, 167.12) * mm});
            skLineSegment(sketch, "E129.trimOffspring", {"start": v(-195, 164.12) * mm, "end": v(-195, 124.62) * mm});
            skLineSegment(sketch, "E130.trimOffspring", {"start": v(-192, 164.12) * mm, "end": v(-192, 124.62) * mm});
            skLineSegment(sketch, "E131.trimOffspring", {"start": v(-192, 164.12) * mm, "end": v(-112, 164.12) * mm});
            skArc(sketch, "E132.trimOffspring", {"start": v(-224.14, 164.12) * mm, "mid": v(-226.35, 159.96) * mm, "end": v(-230.52, 157.76) * mm});
            skLineSegment(sketch, "E133.trimOffspring", {"start": v(-109, 164.12) * mm, "end": v(-69.86, 164.12) * mm});
            skLineSegment(sketch, "E134.trimOffspring", {"start": v(-109, 167.12) * mm, "end": v(-109, 194.12) * mm});
            skLineSegment(sketch, "E135.trimOffspring", {"start": v(-112, 167.12) * mm, "end": v(-192, 167.12) * mm});
            skLineSegment(sketch, "E136.trimOffspring", {"start": v(-112, 164.12) * mm, "end": v(-112, 124.62) * mm});
            skLineSegment(sketch, "E137.trimOffspring", {"start": v(-109, 194.12) * mm, "end": v(-81.7, 194.12) * mm});
            skSolve(sketch);
        }
        {
            var Q0;
            Q0 = qSketchRegion(id + "F25", true);
            extrude(context, id + "F26", {"entities" : qUnion([Q0]), "operationType" : NewBodyOperationType.REMOVE, "oppositeDirection" : true, "depth" : 5 * mm, "offsetDistance" : 25 * mm});
        }
        {
            var Q0;
            Q0=makeQuery(id+"F26.boolean.opBoolean","COPY",EDGE,{"derivedFrom":makeQuery(id+"F26.opExtrude","SWEPT_EDGE",EDGE,{"disambiguationData":[OSD([sQuery(id+"F25.wireOp",EDGE,"E92"),sQuery(id+"F25.wireOp",EDGE,"E102")])]})});
            var Q1;
            Q1=makeQuery(id+"F26.boolean.opBoolean","COPY",EDGE,{"derivedFrom":makeQuery(id+"F26.opExtrude","SWEPT_EDGE",EDGE,{"disambiguationData":[OSD([sQuery(id+"F25.wireOp",EDGE,"E90"),sQuery(id+"F25.wireOp",EDGE,"E103")])]})});
            var Q2;
            Q2=makeQuery(id+"F26.boolean.opBoolean","COPY",EDGE,{"derivedFrom":makeQuery(id+"F26.opExtrude","SWEPT_EDGE",EDGE,{"disambiguationData":[OSD([sQuery(id+"F25.wireOp",EDGE,"E90"),sQuery(id+"F25.wireOp",EDGE,"E123")])]})});
            var Q3;
            Q3=makeQuery(id+"F26.boolean.opBoolean","COPY",EDGE,{"derivedFrom":makeQuery(id+"F26.opExtrude","SWEPT_EDGE",EDGE,{"disambiguationData":[OSD([sQuery(id+"F25.wireOp",EDGE,"E90"),sQuery(id+"F25.wireOp",EDGE,"E124")])]})});
            var Q4;
            Q4=makeQuery(id+"F26.boolean.opBoolean","COPY",EDGE,{"derivedFrom":makeQuery(id+"F26.opExtrude","SWEPT_EDGE",EDGE,{"disambiguationData":[OSD([sQuery(id+"F25.wireOp",EDGE,"E134.trimOffspring"),sQuery(id+"F25.wireOp",EDGE,"E137.trimOffspring")])]})});
            var Q5;
            Q5=makeQuery(id+"F26.boolean.opBoolean","COPY",EDGE,{"derivedFrom":makeQuery(id+"F26.opExtrude","SWEPT_EDGE",EDGE,{"disambiguationData":[OSD([sQuery(id+"F25.wireOp",EDGE,"E104"),sQuery(id+"F25.wireOp",EDGE,"E137.trimOffspring")])]})});
            var Q6;
            Q6=makeQuery(id+"F26.boolean.opBoolean","COPY",EDGE,{"derivedFrom":makeQuery(id+"F26.opExtrude","SWEPT_EDGE",EDGE,{"disambiguationData":[OSD([sQuery(id+"F25.wireOp",EDGE,"E91"),sQuery(id+"F25.wireOp",EDGE,"E105")])]})});
            var Q7;
            Q7=makeQuery(id+"F26.boolean.opBoolean","COPY",EDGE,{"derivedFrom":makeQuery(id+"F26.opExtrude","SWEPT_EDGE",EDGE,{"disambiguationData":[OSD([sQuery(id+"F25.wireOp",EDGE,"E98"),sQuery(id+"F25.wireOp",EDGE,"E133.trimOffspring")])]})});
            var Q8;
            Q8=makeQuery(id+"F26.boolean.opBoolean","COPY",EDGE,{"derivedFrom":makeQuery(id+"F26.opExtrude","SWEPT_EDGE",EDGE,{"disambiguationData":[OSD([sQuery(id+"F25.wireOp",EDGE,"E131.trimOffspring"),sQuery(id+"F25.wireOp",EDGE,"E136.trimOffspring")])]})});
            var Q9;
            Q9=makeQuery(id+"F26.boolean.opBoolean","COPY",EDGE,{"derivedFrom":makeQuery(id+"F26.opExtrude","SWEPT_EDGE",EDGE,{"disambiguationData":[OSD([sQuery(id+"F25.wireOp",EDGE,"E127"),sQuery(id+"F25.wireOp",EDGE,"E129.trimOffspring")])]})});
            var Q10;
            Q10=makeQuery(id+"F26.boolean.opBoolean","COPY",EDGE,{"derivedFrom":makeQuery(id+"F26.opExtrude","SWEPT_EDGE",EDGE,{"disambiguationData":[OSD([sQuery(id+"F25.wireOp",EDGE,"E126"),sQuery(id+"F25.wireOp",EDGE,"E134.trimOffspring")])]})});
            var Q11;
            Q11=makeQuery(id+"F26.boolean.opBoolean","COPY",EDGE,{"derivedFrom":makeQuery(id+"F26.opExtrude","SWEPT_EDGE",EDGE,{"disambiguationData":[OSD([sQuery(id+"F25.wireOp",EDGE,"E98"),sQuery(id+"F25.wireOp",EDGE,"E126")])]})});
            var Q12;
            Q12=makeQuery(id+"F26.boolean.opBoolean","COPY",EDGE,{"derivedFrom":makeQuery(id+"F26.opExtrude","SWEPT_EDGE",EDGE,{"disambiguationData":[OSD([sQuery(id+"F25.wireOp",EDGE,"E116"),sQuery(id+"F25.wireOp",EDGE,"E125")])]})});
            var Q13;
            Q13=makeQuery(id+"F26.boolean.opBoolean","COPY",EDGE,{"derivedFrom":makeQuery(id+"F26.opExtrude","SWEPT_EDGE",EDGE,{"disambiguationData":[OSD([sQuery(id+"F25.wireOp",EDGE,"E97"),sQuery(id+"F25.wireOp",EDGE,"E130.trimOffspring")])]})});
            var Q14;
            Q14=makeQuery(id+"F26.boolean.opBoolean","COPY",EDGE,{"derivedFrom":makeQuery(id+"F26.opExtrude","SWEPT_EDGE",EDGE,{"disambiguationData":[OSD([sQuery(id+"F25.wireOp",EDGE,"E130.trimOffspring"),sQuery(id+"F25.wireOp",EDGE,"E131.trimOffspring")])]})});
            var Q15;
            Q15=makeQuery(id+"F26.boolean.opBoolean","COPY",EDGE,{"derivedFrom":makeQuery(id+"F26.opExtrude","SWEPT_EDGE",EDGE,{"disambiguationData":[OSD([sQuery(id+"F25.wireOp",EDGE,"E127"),sQuery(id+"F25.wireOp",EDGE,"E132.trimOffspring")])]})});
            var Q16;
            Q16=makeQuery(id+"F26.boolean.opBoolean","COPY",EDGE,{"derivedFrom":makeQuery(id+"F26.opExtrude","SWEPT_EDGE",EDGE,{"disambiguationData":[OSD([sQuery(id+"F25.wireOp",EDGE,"E122"),sQuery(id+"F25.wireOp",EDGE,"E128.trimOffspring")])]})});
            var Q17;
            Q17=makeQuery(id+"F26.boolean.opBoolean","COPY",EDGE,{"derivedFrom":makeQuery(id+"F26.opExtrude","SWEPT_EDGE",EDGE,{"disambiguationData":[OSD([sQuery(id+"F25.wireOp",EDGE,"E123"),sQuery(id+"F25.wireOp",EDGE,"E135.trimOffspring")])]})});
            var Q18;
            Q18=makeQuery(id+"F26.boolean.opBoolean","COPY",EDGE,{"derivedFrom":makeQuery(id+"F26.opExtrude","SWEPT_EDGE",EDGE,{"disambiguationData":[OSD([sQuery(id+"F25.wireOp",EDGE,"E93"),sQuery(id+"F25.wireOp",EDGE,"E128.trimOffspring")])]})});
            var Q19;
            Q19=makeQuery(id+"F26.boolean.opBoolean","COPY",EDGE,{"derivedFrom":makeQuery(id+"F26.opExtrude","SWEPT_EDGE",EDGE,{"disambiguationData":[OSD([sQuery(id+"F25.wireOp",EDGE,"E90"),sQuery(id+"F25.wireOp",EDGE,"E122")])]})});
            var Q20;
            Q20=makeQuery(id+"F26.boolean.opBoolean","COPY",EDGE,{"derivedFrom":makeQuery(id+"F26.opExtrude","SWEPT_EDGE",EDGE,{"disambiguationData":[OSD([sQuery(id+"F25.wireOp",EDGE,"E125"),sQuery(id+"F25.wireOp",EDGE,"E133.trimOffspring")])]})});
            var Q21;
            Q21=makeQuery(id+"F26.boolean.opBoolean","COPY",EDGE,{"derivedFrom":makeQuery(id+"F26.opExtrude","SWEPT_EDGE",EDGE,{"disambiguationData":[OSD([sQuery(id+"F25.wireOp",EDGE,"E124"),sQuery(id+"F25.wireOp",EDGE,"E135.trimOffspring")])]})});
            fillet(context, id + "F27", {"entities" : qUnion([Q0, Q1, Q2, Q3, Q4, Q5, Q6, Q7, Q8, Q9, Q10, Q11, Q12, Q13, Q14, Q15, Q16, Q17, Q18, Q19, Q20, Q21]), "radius" : 5 * mm, "tangentPropagation" : true, "allowEdgeOverflow" : false});
        }
        {
            var Q0;
            Q0=makeQuery(id+"F17.boolean.opBoolean","COPY",FACE,{"derivedFrom":makeQuery(id+"F17.opExtrude","CAP_FACE",FACE,{"disambiguationData":[OSD([sQuery(id+"F16.wireOp",EDGE,"E54"),sQuery(id+"F16.wireOp",EDGE,"E55"),sQuery(id+"F16.wireOp",EDGE,"E56"),sQuery(id+"F16.wireOp",EDGE,"E57"),sQuery(id+"F16.wireOp",EDGE,"E58"),sQuery(id+"F16.wireOp",EDGE,"E59"),sQuery(id+"F16.wireOp",EDGE,"E60"),sQuery(id+"F16.wireOp",EDGE,"E61"),sQuery(id+"F16.wireOp",EDGE,"E62"),sQuery(id+"F16.wireOp",EDGE,"E63"),sQuery(id+"F16.wireOp",EDGE,"E64.filletArc"),sQuery(id+"F16.wireOp",EDGE,"E65.filletArc"),sQuery(id+"F16.wireOp",EDGE,"E66.filletArc"),sQuery(id+"F16.wireOp",EDGE,"E67.filletArc"),sQuery(id+"F16.wireOp",EDGE,"E68.filletArc"),sQuery(id+"F16.wireOp",EDGE,"E69.filletArc"),sQuery(id+"F16.wireOp",EDGE,"E70.filletArc"),sQuery(id+"F16.wireOp",EDGE,"E71.filletArc"),sQuery(id+"F16.wireOp",EDGE,"E72.filletArc"),sQuery(id+"F16.wireOp",EDGE,"E73.filletArc")])],"isStart":false})});
            var sketch = newSketch(context, id + "F28", { "sketchPlane" : qUnion([Q0])});
            skArc(sketch, "E138", {"start": v(-218, 193.12) * mm, "mid": v(-222, 189.12) * mm, "end": v(-226, 193.12) * mm});
            skLineSegment(sketch, "E139", {"start": v(-218, 193.12) * mm, "end": v(-218, 196.12) * mm});
            skLineSegment(sketch, "E140", {"start": v(-218, 196.12) * mm, "end": v(-226, 196.12) * mm});
            skLineSegment(sketch, "E141", {"start": v(-226, 196.12) * mm, "end": v(-226, 193.12) * mm});
            skCircle(sketch, "E142", {"center": v(-222, 143.12) * mm, "radius": 4 * mm});
            skCircle(sketch, "E143", {"center": v(-72, 143.12) * mm, "radius": 4 * mm});
            skArc(sketch, "E144", {"start": v(-76, 193.12) * mm, "mid": v(-72, 189.12) * mm, "end": v(-68, 193.12) * mm});
            skLineSegment(sketch, "E145", {"start": v(-68, 193.12) * mm, "end": v(-68, 196.12) * mm});
            skLineSegment(sketch, "E146", {"start": v(-68, 196.12) * mm, "end": v(-76, 196.12) * mm});
            skLineSegment(sketch, "E147", {"start": v(-76, 196.12) * mm, "end": v(-76, 193.12) * mm});
            skSolve(sketch);
        }
        {
            var Q0;
            Q0=makeQuery(id+"F28.imprint","IMPRINT",FACE,{"disambiguationData":[TD([[makeQuery(id+"F28.imprint","IMPRINT",EDGE,{"derivedFrom":sQuery(id+"F28.wireOp",EDGE,"E138")}),1.0]])]});
            extrude(context, id + "F29", {"entities" : qUnion([Q0]), "operationType" : NewBodyOperationType.REMOVE, "oppositeDirection" : true, "depth" : 2 * mm, "offsetDistance" : 25 * mm});
        }
        {
            var Q0;
            Q0=makeQuery(id+"F5.opExtrude","SWEPT_EDGE",EDGE,{"disambiguationData":[OSD([sQuery(id+"F4.wireOp",EDGE,"E9"),sQuery(id+"F4.wireOp",EDGE,"E10")])]});
            var Q1;
            Q1=makeQuery(id+"F5.opExtrude","CAP_EDGE",EDGE,{"disambiguationData":[OSD([sQuery(id+"F4.wireOp",EDGE,"E8")])],"isStart":false});
            var Q2;
            Q2=makeQuery(id+"F5.opExtrude","CAP_EDGE",EDGE,{"disambiguationData":[OSD([sQuery(id+"F4.wireOp",EDGE,"E8")])],"isStart":true});
            var Q3;
            Q3=makeQuery(id+"F5.opExtrude","CAP_EDGE",EDGE,{"disambiguationData":[OSD([sQuery(id+"F4.wireOp",EDGE,"E13")])],"isStart":true});
            var Q4;
            Q4=makeQuery(id+"F5.opExtrude","CAP_EDGE",EDGE,{"disambiguationData":[OSD([sQuery(id+"F4.wireOp",EDGE,"E13")])],"isStart":false});
            var Q5;
            Q5=makeQuery(id+"F5.opExtrude","CAP_EDGE",EDGE,{"disambiguationData":[OSD([sQuery(id+"F4.wireOp",EDGE,"E11")])],"isStart":true});
            var Q6;
            Q6=makeQuery(id+"F5.opExtrude","CAP_EDGE",EDGE,{"disambiguationData":[OSD([sQuery(id+"F4.wireOp",EDGE,"E11")])],"isStart":false});
            fillet(context, id + "F30", {"entities" : qUnion([Q0, Q1, Q2, Q3, Q4, Q5, Q6]), "radius" : 2 * mm, "tangentPropagation" : true, "allowEdgeOverflow" : false});
        }
        {
            var Q0;
            Q0=makeQuery(id+"F5.opExtrude","SWEPT_FACE",FACE,{"disambiguationData":[OSD([sQuery(id+"F4.wireOp",EDGE,"E9")])]});
            var sketch = newSketch(context, id + "F31", { "sketchPlane" : qUnion([Q0])});
            skLineSegment(sketch, "E148.bottom", {"start": v(-95, 183) * mm, "end": v(-84, 183) * mm});
            skLineSegment(sketch, "E148.top", {"start": v(-95, 143) * mm, "end": v(-84, 143) * mm});
            skLineSegment(sketch, "E148.left", {"start": v(-95, 183) * mm, "end": v(-95, 143) * mm});
            skLineSegment(sketch, "E148.right", {"start": v(-84, 183) * mm, "end": v(-84, 143) * mm});
            skSolve(sketch);
        }
        {
            var Q0;
            Q0 = qSketchRegion(id + "F31", true);
            var Q1;
            Q1=makeQuery(id+"F5.opExtrude","SWEPT_FACE",FACE,{"disambiguationData":[OSD([sQuery(id+"F4.wireOp",EDGE,"E16")])]});
            extrude(context, id + "F32", {"entities" : qUnion([Q0]), "operationType" : NewBodyOperationType.REMOVE, "endBound" : BoundingType.UP_TO_SURFACE, "oppositeDirection" : true, "depth" : 25 * mm, "endBoundEntityFace" : qUnion([Q1]), "hasOffset" : true, "offsetDistance" : 4 * mm});
        }
        {
            var Q0;
            Q0=makeQuery(id+"F5.opExtrude","SWEPT_FACE",FACE,{"disambiguationData":[OSD([sQuery(id+"F4.wireOp",EDGE,"E10")])]});
            cPlane(context, id + "F33", {"entities" : qUnion([Q0]), "cplaneType" : CPlaneType.OFFSET, "offset" : 6.5 * mm, "oppositeDirection" : true, "width" : 150 * mm, "height" : 150 * mm});
        }
        {
            var Q0;
            Q0=qCreatedBy(id+"F33.planeOp",FACE);
            var sketch = newSketch(context, id + "F34", { "sketchPlane" : qUnion([Q0])});
            skLineSegment(sketch, "E149.bottom", {"start": v(-95, 190.92) * mm, "end": v(-85.62, 190.92) * mm});
            skLineSegment(sketch, "E149.top", {"start": v(-95, 185.32) * mm, "end": v(-85.62, 185.32) * mm});
            skLineSegment(sketch, "E149.left", {"start": v(-95, 190.92) * mm, "end": v(-95, 185.32) * mm});
            skLineSegment(sketch, "E149.right", {"start": v(-85.62, 190.92) * mm, "end": v(-85.62, 185.32) * mm, "construction": true});
            skLineSegment(sketch, "E150", {"start": v(-85.62, 190.92) * mm, "end": v(-84, 188.12) * mm});
            skLineSegment(sketch, "E151", {"start": v(-84, 188.12) * mm, "end": v(-85.62, 185.32) * mm});
            skLineSegment(sketch, "E152", {"start": v(-84, 188.12) * mm, "end": v(-87.5, 188.12) * mm, "construction": true});
            skLineSegment(sketch, "E153", {"start": v(-124.75, 203.1) * mm, "end": v(-124.75, 166.12) * mm, "construction": true});
            skLineSegment(sketch, "E154", {"start": v(-124.75, 166.12) * mm, "end": v(-36.94, 166.12) * mm, "construction": true});
            skLineSegment(sketch, "E155.MirrorCS", {"start": v(-85.62, 141.32) * mm, "end": v(-84, 144.12) * mm});
            skLineSegment(sketch, "E156.MirrorCS", {"start": v(-84, 144.12) * mm, "end": v(-85.62, 146.92) * mm});
            skLineSegment(sketch, "E157.MirrorCS", {"start": v(-95, 146.92) * mm, "end": v(-85.62, 146.92) * mm});
            skLineSegment(sketch, "E158.MirrorCS", {"start": v(-95, 141.32) * mm, "end": v(-95, 146.92) * mm});
            skLineSegment(sketch, "E159.MirrorCS", {"start": v(-95, 141.32) * mm, "end": v(-85.62, 141.32) * mm});
            skLineSegment(sketch, "E160.MirrorCS", {"start": v(-154.5, 141.32) * mm, "end": v(-154.5, 146.92) * mm, "construction": true});
            skLineSegment(sketch, "E161.MirrorCS", {"start": v(-154.5, 141.32) * mm, "end": v(-163.88, 141.32) * mm});
            skLineSegment(sketch, "E162.MirrorCS", {"start": v(-163.88, 141.32) * mm, "end": v(-165.5, 144.12) * mm});
            skLineSegment(sketch, "E163.MirrorCS", {"start": v(-165.5, 144.12) * mm, "end": v(-163.88, 146.92) * mm});
            skLineSegment(sketch, "E164.MirrorCS", {"start": v(-154.5, 146.92) * mm, "end": v(-163.88, 146.92) * mm});
            skLineSegment(sketch, "E165.MirrorCS", {"start": v(-154.5, 190.92) * mm, "end": v(-154.5, 185.32) * mm, "construction": true});
            skLineSegment(sketch, "E166.MirrorCS", {"start": v(-154.5, 185.32) * mm, "end": v(-163.88, 185.32) * mm});
            skLineSegment(sketch, "E167.MirrorCS", {"start": v(-165.5, 188.12) * mm, "end": v(-163.88, 185.32) * mm});
            skLineSegment(sketch, "E168.MirrorCS", {"start": v(-163.88, 190.92) * mm, "end": v(-165.5, 188.12) * mm});
            skLineSegment(sketch, "E169.MirrorCS", {"start": v(-154.5, 190.92) * mm, "end": v(-163.88, 190.92) * mm});
            skLineSegment(sketch, "E170", {"start": v(-154.5, 190.92) * mm, "end": v(-144.5, 190.92) * mm});
            skLineSegment(sketch, "E171", {"start": v(-144.5, 190.92) * mm, "end": v(-144.5, 185.32) * mm});
            skLineSegment(sketch, "E172", {"start": v(-144.5, 185.32) * mm, "end": v(-154.5, 185.32) * mm});
            skLineSegment(sketch, "E173", {"start": v(-154.5, 146.92) * mm, "end": v(-144.5, 146.92) * mm});
            skLineSegment(sketch, "E174", {"start": v(-144.5, 146.92) * mm, "end": v(-144.5, 141.32) * mm});
            skLineSegment(sketch, "E175", {"start": v(-144.5, 141.32) * mm, "end": v(-154.5, 141.32) * mm});
            skSolve(sketch);
        }
        {
            var Q0;
            Q0 = qSketchRegion(id + "F34", true);
            extrude(context, id + "F35", {"entities" : qUnion([Q0]), "operationType" : NewBodyOperationType.REMOVE, "oppositeDirection" : true, "depth" : 3.5 * mm, "offsetDistance" : 25 * mm});
        }
        {
            var Q0;
            Q0=makeQuery(id+"F5.opExtrude","CAP_FACE",FACE,{"disambiguationData":[OSD([sQuery(id+"F4.wireOp",EDGE,"E8"),sQuery(id+"F4.wireOp",EDGE,"E9"),sQuery(id+"F4.wireOp",EDGE,"E10"),sQuery(id+"F4.wireOp",EDGE,"E11"),sQuery(id+"F4.wireOp",EDGE,"E12"),sQuery(id+"F4.wireOp",EDGE,"E13"),sQuery(id+"F4.wireOp",EDGE,"E14"),sQuery(id+"F4.wireOp",EDGE,"E15"),sQuery(id+"F4.wireOp",EDGE,"E16")])],"isStart":false});
            var sketch = newSketch(context, id + "F36", { "sketchPlane" : qUnion([Q0])});
            skLineSegment(sketch, "E176", {"start": v(-30.04, 226.39) * mm, "end": v(-8.55, 204.89) * mm});
            skLineSegment(sketch, "E177", {"start": v(-8.55, 202.06) * mm, "end": v(-11.38, 199.23) * mm});
            skLineSegment(sketch, "E178", {"start": v(-11.38, 196.4) * mm, "end": v(-4.59, 189.62) * mm});
            skLineSegment(sketch, "E179", {"start": v(-4, 188.2) * mm, "end": v(-4, 172) * mm});
            skLineSegment(sketch, "E180", {"start": v(-10.82, 142) * mm, "end": v(-18.66, 165.36) * mm});
            skLineSegment(sketch, "E181", {"start": v(-36.7, 222.56) * mm, "end": v(-32.87, 226.39) * mm});
            skPoint(sketch, "E182.visualSharp", {"position": v(-4, 121.7) * mm});
            skArc(sketch, "E182.filletArc", {"start": v(-10.82, 142) * mm, "mid": v(-6.94, 139.66) * mm, "end": v(-4, 143.11) * mm});
            skPoint(sketch, "E183.visualSharp", {"position": v(-37.58, 221.68) * mm});
            skArc(sketch, "E183.filletArc", {"start": v(-36.7, 222.56) * mm, "mid": v(-37.23, 221.6) * mm, "end": v(-37.18, 220.5) * mm});
            skPoint(sketch, "E184.visualSharp", {"position": v(-31.46, 227.8) * mm});
            skArc(sketch, "E184.filletArc", {"start": v(-30.04, 226.39) * mm, "mid": v(-31.46, 226.97) * mm, "end": v(-32.87, 226.39) * mm});
            skPoint(sketch, "E185.visualSharp", {"position": v(-7.13, 203.48) * mm});
            skArc(sketch, "E185.filletArc", {"start": v(-8.55, 202.06) * mm, "mid": v(-7.96, 203.48) * mm, "end": v(-8.55, 204.89) * mm});
            skPoint(sketch, "E186.visualSharp", {"position": v(-12.79, 197.82) * mm});
            skArc(sketch, "E186.filletArc", {"start": v(-11.38, 199.23) * mm, "mid": v(-11.96, 197.82) * mm, "end": v(-11.38, 196.4) * mm});
            skPoint(sketch, "E187.visualSharp", {"position": v(-4, 189.03) * mm});
            skArc(sketch, "E187.filletArc", {"start": v(-4, 188.2) * mm, "mid": v(-4.15, 188.97) * mm, "end": v(-4.59, 189.62) * mm});
            skLineSegment(sketch, "E188", {"start": v(-18.78, 170) * mm, "end": v(-6, 170) * mm});
            skLineSegment(sketch, "E189", {"start": v(-6, 168) * mm, "end": v(-16.77, 168) * mm});
            skLineSegment(sketch, "E190.trimOffspring", {"start": v(-20.68, 171.36) * mm, "end": v(-37.18, 220.5) * mm});
            skPoint(sketch, "E191.visualSharp", {"position": v(-20.22, 170) * mm});
            skArc(sketch, "E191.filletArc", {"start": v(-20.68, 171.36) * mm, "mid": v(-19.95, 170.38) * mm, "end": v(-18.78, 170) * mm});
            skPoint(sketch, "E192.visualSharp", {"position": v(-19.55, 168) * mm});
            skArc(sketch, "E192.filletArc", {"start": v(-16.77, 168) * mm, "mid": v(-18.4, 167.17) * mm, "end": v(-18.66, 165.36) * mm});
            skLineSegment(sketch, "E193.trimOffspring", {"start": v(-4, 166) * mm, "end": v(-4, 143.11) * mm});
            skPoint(sketch, "E194.visualSharp", {"position": v(-4, 170) * mm});
            skArc(sketch, "E194.filletArc", {"start": v(-6, 170) * mm, "mid": v(-4.59, 170.59) * mm, "end": v(-4, 172) * mm});
            skPoint(sketch, "E195.visualSharp", {"position": v(-4, 168) * mm});
            skArc(sketch, "E195.filletArc", {"start": v(-4, 166) * mm, "mid": v(-4.59, 167.41) * mm, "end": v(-6, 168) * mm});
            skSolve(sketch);
        }
        {
            var Q0;
            Q0 = qSketchRegion(id + "F36", true);
            var Q1;
            Q1=makeQuery(id+"F5.opExtrude","CAP_FACE",FACE,{"disambiguationData":[OSD([sQuery(id+"F4.wireOp",EDGE,"E8"),sQuery(id+"F4.wireOp",EDGE,"E9"),sQuery(id+"F4.wireOp",EDGE,"E10"),sQuery(id+"F4.wireOp",EDGE,"E11"),sQuery(id+"F4.wireOp",EDGE,"E12"),sQuery(id+"F4.wireOp",EDGE,"E13"),sQuery(id+"F4.wireOp",EDGE,"E14"),sQuery(id+"F4.wireOp",EDGE,"E15"),sQuery(id+"F4.wireOp",EDGE,"E16")])],"isStart":true});
            extrude(context, id + "F37", {"entities" : qUnion([Q0]), "operationType" : NewBodyOperationType.REMOVE, "endBound" : BoundingType.UP_TO_SURFACE, "oppositeDirection" : true, "depth" : 25 * mm, "endBoundEntityFace" : qUnion([Q1]), "hasOffset" : true, "offsetDistance" : 3 * mm});
        }
        {
            var Q0;
            Q0=makeQuery(id+"F32.boolean.opBoolean","COPY",EDGE,{"derivedFrom":makeQuery(id+"F32.opExtrude","CAP_EDGE",EDGE,{"disambiguationData":[OSD([sQuery(id+"F31.wireOp",EDGE,"E148.bottom")])],"isStart":false})});
            var Q1;
            Q1=makeQuery(id+"F32.boolean.opBoolean","COPY",EDGE,{"derivedFrom":makeQuery(id+"F32.opExtrude","SWEPT_EDGE",EDGE,{"disambiguationData":[OSD([sQuery(id+"F31.wireOp",EDGE,"E148.bottom"),sQuery(id+"F31.wireOp",EDGE,"E148.right")])]})});
            var Q2;
            Q2=makeQuery(id+"F32.boolean.opBoolean","COPY",EDGE,{"derivedFrom":makeQuery(id+"F32.opExtrude","CAP_EDGE",EDGE,{"disambiguationData":[OSD([sQuery(id+"F31.wireOp",EDGE,"E148.top")])],"isStart":false})});
            var Q3;
            Q3=makeQuery(id+"F32.boolean.opBoolean","COPY",EDGE,{"derivedFrom":makeQuery(id+"F32.opExtrude","CAP_EDGE",EDGE,{"disambiguationData":[OSD([sQuery(id+"F31.wireOp",EDGE,"E148.right")])],"isStart":false})});
            var Q4;
            Q4=makeQuery(id+"F32.boolean.opBoolean","COPY",EDGE,{"derivedFrom":makeQuery(id+"F32.opExtrude","SWEPT_EDGE",EDGE,{"disambiguationData":[OSD([sQuery(id+"F31.wireOp",EDGE,"E148.top"),sQuery(id+"F31.wireOp",EDGE,"E148.right")])]})});
            fillet(context, id + "F38", {"entities" : qUnion([Q0, Q1, Q2, Q3, Q4]), "radius" : 2 * mm, "tangentPropagation" : true, "allowEdgeOverflow" : false});
        }
        {
            var Q0;
            Q0=makeQuery(id+"F5.opExtrude","CAP_FACE",FACE,{"disambiguationData":[OSD([sQuery(id+"F4.wireOp",EDGE,"E8"),sQuery(id+"F4.wireOp",EDGE,"E9"),sQuery(id+"F4.wireOp",EDGE,"E10"),sQuery(id+"F4.wireOp",EDGE,"E11"),sQuery(id+"F4.wireOp",EDGE,"E12"),sQuery(id+"F4.wireOp",EDGE,"E13"),sQuery(id+"F4.wireOp",EDGE,"E14"),sQuery(id+"F4.wireOp",EDGE,"E15"),sQuery(id+"F4.wireOp",EDGE,"E16")])],"isStart":false});
            var sketch = newSketch(context, id + "F39", { "sketchPlane" : qUnion([Q0])});
            skLineSegment(sketch, "E196.bottom", {"start": v(-8, 136.8) * mm, "end": v(-4, 136.8) * mm});
            skLineSegment(sketch, "E196.top", {"start": v(-8, 131.2) * mm, "end": v(-4, 131.2) * mm});
            skLineSegment(sketch, "E196.left", {"start": v(-8, 136.8) * mm, "end": v(-8, 131.2) * mm});
            skLineSegment(sketch, "E196.right", {"start": v(-4, 136.8) * mm, "end": v(-4, 131.2) * mm});
            skLineSegment(sketch, "E197", {"start": v(15, 134) * mm, "end": v(-4, 134) * mm, "construction": true});
            skSolve(sketch);
        }
        {
            var Q0;
            Q0 = qSketchRegion(id + "F39", true);
            extrude(context, id + "F40", {"entities" : qUnion([Q0]), "operationType" : NewBodyOperationType.REMOVE, "oppositeDirection" : true, "depth" : (7.5 + 3.5 + 5.6 / 2) * mm, "offsetDistance" : 25 * mm});
        }
        {
            var Q0;
            Q0=makeQuery(id+"F40.boolean.opBoolean","COPY",EDGE,{"derivedFrom":makeQuery(id+"F40.opExtrude","CAP_EDGE",EDGE,{"disambiguationData":[OSD([sQuery(id+"F39.wireOp",EDGE,"E196.bottom")])],"isStart":false})});
            var Q1;
            Q1=makeQuery(id+"F40.boolean.opBoolean","COPY",EDGE,{"derivedFrom":makeQuery(id+"F40.opExtrude","CAP_EDGE",EDGE,{"disambiguationData":[OSD([sQuery(id+"F39.wireOp",EDGE,"E196.top")])],"isStart":false})});
            chamfer(context, id + "F41", {"entities" : qUnion([Q0, Q1]), "chamferType" : ChamferType.OFFSET_ANGLE, "width" : (5.6 / 2) * mm, "oppositeDirection" : true, "angle" : 30 * degree, "tangentPropagation" : true});
        }
        {
            var Q0;
            Q0=makeQuery(id+"F20.opExtrude","SWEPT_FACE",FACE,{"disambiguationData":[OSD([sQuery(id+"F19.wireOp",EDGE,"E75")])]});
            var sketch = newSketch(context, id + "F42", { "sketchPlane" : qUnion([Q0])});
            skCircle(sketch, "E198", {"center": v(-172, 172) * mm, "radius": 1.75 * mm});
            skCircle(sketch, "E199", {"center": v(-152, 172) * mm, "radius": 1.75 * mm});
            skSolve(sketch);
        }
        {
            var Q0;
            Q0=makeQuery(id+"F42.imprint","IMPRINT",FACE,{"disambiguationData":[TD([[makeQuery(id+"F42.imprint","IMPRINT",EDGE,{"derivedFrom":sQuery(id+"F42.wireOp",EDGE,"E198")}),1.0]])]});
            var Q1;
            Q1=makeQuery(id+"F42.imprint","IMPRINT",FACE,{"disambiguationData":[TD([[makeQuery(id+"F42.imprint","IMPRINT",EDGE,{"derivedFrom":sQuery(id+"F42.wireOp",EDGE,"E199")}),1.0]])]});
            extrude(context, id + "F43", {"entities" : qUnion([Q0, Q1]), "operationType" : NewBodyOperationType.REMOVE, "oppositeDirection" : true, "depth" : 25 * mm, "offsetDistance" : 25 * mm});
        }
        {
            var Q0;
            Q0=makeQuery(id+"F20.opExtrude","CAP_FACE",FACE,{"disambiguationData":[OSD([sQuery(id+"F19.wireOp",EDGE,"E74"),sQuery(id+"F19.wireOp",EDGE,"E75"),sQuery(id+"F19.wireOp",EDGE,"E76"),sQuery(id+"F19.wireOp",EDGE,"E77"),sQuery(id+"F19.wireOp",EDGE,"E78"),sQuery(id+"F19.wireOp",EDGE,"E79"),sQuery(id+"F19.wireOp",EDGE,"E80")])],"isStart":true});
            var sketch = newSketch(context, id + "F44", { "sketchPlane" : qUnion([Q0])});
            skLineSegment(sketch, "E200", {"start": v(44.4, 229.43) * mm, "end": v(6, 144.22) * mm});
            skLineSegment(sketch, "E201", {"start": v(6, 144.22) * mm, "end": v(6, 182.75) * mm});
            skLineSegment(sketch, "E202", {"start": v(11.86, 196.89) * mm, "end": v(44.4, 229.43) * mm});
            skPoint(sketch, "E203.visualSharp", {"position": v(6, 191.03) * mm});
            skArc(sketch, "E203.filletArc", {"start": v(11.86, 196.89) * mm, "mid": v(7.52, 190.4) * mm, "end": v(6, 182.75) * mm});
            skSolve(sketch);
        }
        {
            var Q0;
            Q0 = qSketchRegion(id + "F44", true);
            var Q1;
            Q1=makeQuery(id+"F20.opExtrude","CAP_FACE",FACE,{"disambiguationData":[OSD([sQuery(id+"F19.wireOp",EDGE,"E74"),sQuery(id+"F19.wireOp",EDGE,"E75"),sQuery(id+"F19.wireOp",EDGE,"E76"),sQuery(id+"F19.wireOp",EDGE,"E77"),sQuery(id+"F19.wireOp",EDGE,"E78"),sQuery(id+"F19.wireOp",EDGE,"E79"),sQuery(id+"F19.wireOp",EDGE,"E80")])],"isStart":false});
            extrude(context, id + "F45", {"entities" : qUnion([Q0]), "operationType" : NewBodyOperationType.REMOVE, "endBound" : BoundingType.UP_TO_SURFACE, "oppositeDirection" : true, "depth" : 25 * mm, "endBoundEntityFace" : qUnion([Q1]), "hasOffset" : true, "offsetDistance" : 2.5 * mm});
        }
        {
            var Q0;
            Q0=makeQuery(id+"F20.opExtrude","CAP_FACE",FACE,{"disambiguationData":[OSD([sQuery(id+"F19.wireOp",EDGE,"E74"),sQuery(id+"F19.wireOp",EDGE,"E75"),sQuery(id+"F19.wireOp",EDGE,"E76"),sQuery(id+"F19.wireOp",EDGE,"E77"),sQuery(id+"F19.wireOp",EDGE,"E78"),sQuery(id+"F19.wireOp",EDGE,"E79"),sQuery(id+"F19.wireOp",EDGE,"E80")])],"isStart":true});
            var sketch = newSketch(context, id + "F46", { "sketchPlane" : qUnion([Q0])});
            skLineSegment(sketch, "E204", {"start": v(54.85, 228.8) * mm, "end": v(42.94, 240.7) * mm});
            skLineSegment(sketch, "E205", {"start": v(42.94, 240.7) * mm, "end": v(-1.78, 195.98) * mm});
            skPoint(sketch, "E205.endSnap0", {"position": v(4.76, 195.1) * mm});
            skLineSegment(sketch, "E206", {"start": v(-1.78, 195.98) * mm, "end": v(6, 188.2) * mm});
            skLineSegment(sketch, "E207", {"start": v(54.85, 228.8) * mm, "end": v(6, 182.75) * mm});
            skLineSegment(sketch, "E208", {"start": v(6, 188.2) * mm, "end": v(6, 182.75) * mm});
            skSolve(sketch);
        }
        {
            var Q0;
            {var subQ2=sQuery(id+"F46.wireOp",EDGE,"E206");Q0=makeQuery(id+"F46.imprint","IMPRINT",FACE,{"disambiguationData":[TD([[makeQuery(id+"F46.imprint","IMPRINT",EDGE,{"derivedFrom":subQ2}),1.0]])]});}
            extrude(context, id + "F47", {"entities" : qUnion([Q0]), "operationType" : NewBodyOperationType.REMOVE, "oppositeDirection" : true, "depth" : 10 * mm, "offsetDistance" : 25 * mm});
        }
        {
            var Q0;
            Q0=makeQuery(id+"F47.boolean.opBoolean","COPY",FACE,{"derivedFrom":makeQuery(id+"F47.opExtrude","CAP_FACE",FACE,{"disambiguationData":[OSD([sQuery(id+"F34.wireOp",EDGE,"E170"),sQuery(id+"F34.wireOp",EDGE,"E171"),sQuery(id+"F34.wireOp",EDGE,"E172"),sQuery(id+"F34.wireOp",EDGE,"E173"),sQuery(id+"F34.wireOp",EDGE,"E174"),sQuery(id+"F34.wireOp",EDGE,"E175"),sQuery(id+"F44.wireOp",EDGE,"E201"),sQuery(id+"F44.wireOp",EDGE,"E202"),sQuery(id+"F44.wireOp",EDGE,"E203.filletArc"),sQuery(id+"F46.wireOp",EDGE,"E204"),sQuery(id+"F46.wireOp",EDGE,"E205"),sQuery(id+"F46.wireOp",EDGE,"E206")])],"isStart":false})});
            var sketch = newSketch(context, id + "F48", { "sketchPlane" : qUnion([Q0])});
            skLineSegment(sketch, "E209", {"start": v(36.4, 221.44) * mm, "end": v(30.04, 227.8) * mm});
            skLineSegment(sketch, "E210", {"start": v(30.04, 227.8) * mm, "end": v(7.13, 204.89) * mm});
            skLineSegment(sketch, "E211", {"start": v(7.13, 204.89) * mm, "end": v(13.5, 198.53) * mm});
            skLineSegment(sketch, "E212", {"start": v(13.5, 198.53) * mm, "end": v(36.4, 221.44) * mm});
            skPoint(sketch, "E213.firstSnap0", {"position": v(2.11, 192.1) * mm});
            skLineSegment(sketch, "E213.bottom", {"start": v(3, 191.2) * mm, "end": v(11, 191.2) * mm});
            skLineSegment(sketch, "E213.top", {"start": v(3, 176) * mm, "end": v(11, 176) * mm});
            skLineSegment(sketch, "E213.left", {"start": v(3, 191.2) * mm, "end": v(3, 176) * mm});
            skLineSegment(sketch, "E213.right", {"start": v(11, 191.2) * mm, "end": v(11, 176) * mm});
            skLineSegment(sketch, "E214.bottom", {"start": v(3, 168) * mm, "end": v(11, 168) * mm});
            skLineSegment(sketch, "E214.top", {"start": v(3, 144) * mm, "end": v(11, 144) * mm});
            skLineSegment(sketch, "E214.left", {"start": v(3, 168) * mm, "end": v(3, 144) * mm});
            skLineSegment(sketch, "E214.right", {"start": v(11, 168) * mm, "end": v(11, 144) * mm});
            skSolve(sketch);
        }
        {
            var Q0;
            Q0 = qSketchRegion(id + "F48", true);
            extrude(context, id + "F49", {"entities" : qUnion([Q0]), "operationType" : NewBodyOperationType.REMOVE, "oppositeDirection" : true, "depth" : 15 * mm, "offsetDistance" : 25 * mm, "hasSecondDirection" : true, "secondDirectionOppositeDirection" : false, "secondDirectionDepth" : 25 * mm});
        }
        {
            var Q0;
            Q0=makeQuery(id+"F49.boolean.opBoolean","COPY",EDGE,{"derivedFrom":makeQuery(id+"F49.opExtrude","SWEPT_EDGE",EDGE,{"disambiguationData":[OSD([sQuery(id+"F46.wireOp",EDGE,"E205"),sQuery(id+"F48.wireOp",EDGE,"E209"),sQuery(id+"F48.wireOp",EDGE,"E210")])]})});
            var Q1;
            Q1=makeQuery(id+"F49.boolean.opBoolean","COPY",EDGE,{"derivedFrom":makeQuery(id+"F49.opExtrude","SWEPT_EDGE",EDGE,{"disambiguationData":[OSD([sQuery(id+"F46.wireOp",EDGE,"E205"),sQuery(id+"F48.wireOp",EDGE,"E210"),sQuery(id+"F48.wireOp",EDGE,"E211")])]})});
            var Q2;
            Q2=makeQuery(id+"F47.boolean.opBoolean","COPY",EDGE,{"derivedFrom":makeQuery(id+"F47.opExtrude","SWEPT_EDGE",EDGE,{"disambiguationData":[OSD([sQuery(id+"F46.wireOp",EDGE,"E205"),sQuery(id+"F46.wireOp",EDGE,"E206")])]})});
            var Q3;
            {var subQ0=sQuery(id+"F48.wireOp",EDGE,"E213.bottom");var subQ1=sQuery(id+"F48.wireOp",EDGE,"E213.left");Q3=makeQuery(id+"F49.boolean.opBoolean","COPY",EDGE,{"disambiguationData":[topologyDisambiguationEdgeConnected([makeQuery(id+"F49.opExtrude","SWEPT_FACE",FACE,{"disambiguationData":[OSD([subQ0])]})])],"derivedFrom":makeQuery(id+"F49.opExtrude","SWEPT_EDGE",EDGE,{"disambiguationData":[OSD([sQuery(id+"F46.wireOp",EDGE,"E206"),subQ0,subQ1])]})});}
            var Q4;
            Q4=makeQuery(id+"F49.boolean.opBoolean","COPY",EDGE,{"derivedFrom":makeQuery(id+"F49.opExtrude","SWEPT_EDGE",EDGE,{"disambiguationData":[OSD([sQuery(id+"F48.wireOp",EDGE,"E213.top"),sQuery(id+"F48.wireOp",EDGE,"E213.left")])]})});
            var Q5;
            Q5=makeQuery(id+"F49.boolean.opBoolean","COPY",EDGE,{"derivedFrom":makeQuery(id+"F49.opExtrude","SWEPT_EDGE",EDGE,{"disambiguationData":[OSD([sQuery(id+"F48.wireOp",EDGE,"E214.bottom"),sQuery(id+"F48.wireOp",EDGE,"E214.left")])]})});
            var Q6;
            Q6=makeQuery(id+"F49.boolean.opBoolean","COPY",EDGE,{"derivedFrom":makeQuery(id+"F49.opExtrude","SWEPT_EDGE",EDGE,{"disambiguationData":[OSD([sQuery(id+"F48.wireOp",EDGE,"E214.top"),sQuery(id+"F48.wireOp",EDGE,"E214.left")])]})});
            var Q7;
            Q7=makeQuery(id+"F47.boolean.opBoolean","COPY",EDGE,{"derivedFrom":makeQuery(id+"F47.opExtrude","SWEPT_EDGE",EDGE,{"disambiguationData":[OSD([sQuery(id+"F46.wireOp",EDGE,"E205"),sQuery(id+"F46.wireOp",EDGE,"E206")])]})});
            fillet(context, id + "F50", {"entities" : qUnion([Q0, Q1, Q2, Q3, Q4, Q5, Q6, Q7]), "radius" : 4 * mm, "tangentPropagation" : true, "allowEdgeOverflow" : false});
        }
        {
            var Q0;
            Q0=makeQuery(id+"F45.boolean.opBoolean","COPY",EDGE,{"derivedFrom":makeQuery(id+"F45.opExtrude","CAP_EDGE",EDGE,{"disambiguationData":[OSD([sQuery(id+"F44.wireOp",EDGE,"E202")])],"isStart":false})});
            var Q1;
            {var subQ0=sQuery(id+"F46.wireOp",EDGE,"E206");var subQ1=sQuery(id+"F48.wireOp",EDGE,"E213.left");Q1=makeQuery(id+"F49.boolean.opBoolean","COPY",EDGE,{"disambiguationData":[topologyDisambiguationEdgeConnected([makeQuery(id+"F47.boolean.opBoolean","COPY",FACE,{"derivedFrom":makeQuery(id+"F47.opExtrude","SWEPT_FACE",FACE,{"disambiguationData":[OSD([subQ0])]})})])],"derivedFrom":makeQuery(id+"F49.opExtrude","SWEPT_EDGE",EDGE,{"disambiguationData":[OSD([subQ0,sQuery(id+"F48.wireOp",EDGE,"E213.bottom"),subQ1])]})});}
            fillet(context, id + "F51", {"entities" : qUnion([Q0, Q1]), "radius" : 2 * mm, "tangentPropagation" : true, "allowEdgeOverflow" : false});
        }
        {
            var Q0;
            Q0=makeQuery(id+"F45.boolean.opBoolean","COPY",EDGE,{"derivedFrom":makeQuery(id+"F45.opExtrude","CAP_EDGE",EDGE,{"disambiguationData":[OSD([sQuery(id+"F44.wireOp",EDGE,"E202")])],"isStart":false})});
            var Q1;
            Q1=makeQuery(id+"F49.boolean.opBoolean","COPY",EDGE,{"derivedFrom":makeQuery(id+"F49.opExtrude","CAP_EDGE",EDGE,{"disambiguationData":[OSD([sQuery(id+"F48.wireOp",EDGE,"E210")])],"isStart":false})});
            var Q2;
            {var subQ0=sQuery(id+"F46.wireOp",EDGE,"E206");var subQ1=sQuery(id+"F46.wireOp",EDGE,"E205");Q2=makeQuery(id+"F49.boolean.opBoolean","SPLIT",EDGE,{"disambiguationData":[TD([makeQuery(id+"F47.boolean.opBoolean","COPY",FACE,{"derivedFrom":makeQuery(id+"F47.opExtrude","SWEPT_FACE",FACE,{"disambiguationData":[OSD([subQ0])]})})])],"derivedFrom":makeQuery(id+"F47.boolean.opBoolean","COPY",EDGE,{"derivedFrom":makeQuery(id+"F47.opExtrude","CAP_EDGE",EDGE,{"disambiguationData":[OSD([subQ1])],"isStart":false})})});}
            var Q3;
            {var subQ0=sQuery(id+"F48.wireOp",EDGE,"E213.left");var subQ1=sQuery(id+"F48.wireOp",EDGE,"E213.bottom");Q3=makeQuery(id+"F50.opFillet","BLEND_EDGE",EDGE,{"blendedFrom":[makeQuery(id+"F49.boolean.opBoolean","COPY",EDGE,{"disambiguationData":[topologyDisambiguationEdgeConnected([makeQuery(id+"F49.opExtrude","SWEPT_FACE",FACE,{"disambiguationData":[OSD([subQ1])]})])],"derivedFrom":makeQuery(id+"F49.opExtrude","SWEPT_EDGE",EDGE,{"disambiguationData":[OSD([sQuery(id+"F46.wireOp",EDGE,"E206"),subQ1,subQ0])]})}),makeQuery(id+"F49.boolean.opBoolean","COPY",FACE,{"derivedFrom":makeQuery(id+"F49.opExtrude","CAP_FACE",FACE,{"disambiguationData":[OSD([subQ1,sQuery(id+"F48.wireOp",EDGE,"E213.top"),subQ0,sQuery(id+"F48.wireOp",EDGE,"E213.right")])],"isStart":false})})],"blendedInto":[makeQuery(id+"F49.boolean.opBoolean","COPY",FACE,{"derivedFrom":makeQuery(id+"F49.opExtrude","CAP_FACE",FACE,{"disambiguationData":[OSD([subQ1,sQuery(id+"F48.wireOp",EDGE,"E213.top"),subQ0,sQuery(id+"F48.wireOp",EDGE,"E213.right")])],"isStart":false})})]});}
            var Q4;
            {var subQ0=sQuery(id+"F48.wireOp",EDGE,"E214.left");var subQ1=sQuery(id+"F48.wireOp",EDGE,"E214.bottom");Q4=makeQuery(id+"F50.opFillet","BLEND_EDGE",EDGE,{"blendedFrom":[makeQuery(id+"F49.boolean.opBoolean","COPY",EDGE,{"derivedFrom":makeQuery(id+"F49.opExtrude","SWEPT_EDGE",EDGE,{"disambiguationData":[OSD([subQ1,subQ0])]})}),makeQuery(id+"F49.boolean.opBoolean","COPY",FACE,{"derivedFrom":makeQuery(id+"F49.opExtrude","CAP_FACE",FACE,{"disambiguationData":[OSD([subQ1,sQuery(id+"F48.wireOp",EDGE,"E214.top"),subQ0,sQuery(id+"F48.wireOp",EDGE,"E214.right")])],"isStart":false})})],"blendedInto":[makeQuery(id+"F49.boolean.opBoolean","COPY",FACE,{"derivedFrom":makeQuery(id+"F49.opExtrude","CAP_FACE",FACE,{"disambiguationData":[OSD([subQ1,sQuery(id+"F48.wireOp",EDGE,"E214.top"),subQ0,sQuery(id+"F48.wireOp",EDGE,"E214.right")])],"isStart":false})})]});}
            var Q5;
            {var subQ0=sQuery(id+"F34.wireOp",EDGE,"E172");var subQ1=sQuery(id+"F34.wireOp",EDGE,"E171");var subQ2=sQuery(id+"F34.wireOp",EDGE,"E170");var subQ7=sQuery(id+"F44.wireOp",EDGE,"E202");var subQ8=sQuery(id+"F46.wireOp",EDGE,"E204");var subQ9=sQuery(id+"F46.wireOp",EDGE,"E205");Q5=makeQuery(id+"F50.opFillet","BLEND_EDGE",EDGE,{"blendedFrom":[makeQuery(id+"F47.boolean.opBoolean","COPY",EDGE,{"derivedFrom":makeQuery(id+"F47.opExtrude","SWEPT_EDGE",EDGE,{"disambiguationData":[OSD([subQ8,subQ9])]})}),makeQuery(id+"F49.boolean.opBoolean","SPLIT",FACE,{"disambiguationData":[TD([makeQuery(id+"F20.opExtrude","SWEPT_FACE",FACE,{"disambiguationData":[OSD([sQuery(id+"F19.wireOp",EDGE,"E77")])]})])],"derivedFrom":makeQuery(id+"F47.boolean.opBoolean","COPY",FACE,{"derivedFrom":makeQuery(id+"F47.opExtrude","CAP_FACE",FACE,{"disambiguationData":[OSD([subQ2,subQ1,subQ0,sQuery(id+"F34.wireOp",EDGE,"E173"),sQuery(id+"F34.wireOp",EDGE,"E174"),sQuery(id+"F34.wireOp",EDGE,"E175"),sQuery(id+"F44.wireOp",EDGE,"E201"),subQ7,sQuery(id+"F44.wireOp",EDGE,"E203.filletArc"),subQ8,subQ9,sQuery(id+"F46.wireOp",EDGE,"E206")])],"isStart":false})})})],"blendedInto":[makeQuery(id+"F49.boolean.opBoolean","SPLIT",FACE,{"disambiguationData":[TD([makeQuery(id+"F20.opExtrude","SWEPT_FACE",FACE,{"disambiguationData":[OSD([sQuery(id+"F19.wireOp",EDGE,"E77")])]})])],"derivedFrom":makeQuery(id+"F47.boolean.opBoolean","COPY",FACE,{"derivedFrom":makeQuery(id+"F47.opExtrude","CAP_FACE",FACE,{"disambiguationData":[OSD([subQ2,subQ1,subQ0,sQuery(id+"F34.wireOp",EDGE,"E173"),sQuery(id+"F34.wireOp",EDGE,"E174"),sQuery(id+"F34.wireOp",EDGE,"E175"),sQuery(id+"F44.wireOp",EDGE,"E201"),subQ7,sQuery(id+"F44.wireOp",EDGE,"E203.filletArc"),subQ8,subQ9,sQuery(id+"F46.wireOp",EDGE,"E206")])],"isStart":false})})})]});}
            fillet(context, id + "F52", {"entities" : qUnion([Q0, Q1, Q2, Q3, Q4, Q5]), "radius" : 2 * mm, "tangentPropagation" : true, "allowEdgeOverflow" : false});
        }
        {
            var Q0;
            Q0=makeQuery(id+"F20.opExtrude","CAP_EDGE",EDGE,{"disambiguationData":[OSD([sQuery(id+"F19.wireOp",EDGE,"E79")])],"isStart":false});
            var Q1;
            Q1=makeQuery(id+"F20.opExtrude","SWEPT_EDGE",EDGE,{"disambiguationData":[OSD([sQuery(id+"F19.wireOp",EDGE,"E74"),sQuery(id+"F19.wireOp",EDGE,"E80")])]});
            var Q2;
            Q2=makeQuery(id+"F20.opExtrude","SWEPT_EDGE",EDGE,{"disambiguationData":[OSD([sQuery(id+"F19.wireOp",EDGE,"E77"),sQuery(id+"F19.wireOp",EDGE,"E78")])]});
            fillet(context, id + "F53", {"entities" : qUnion([Q0, Q1, Q2]), "radius" : 2 * mm, "tangentPropagation" : true, "allowEdgeOverflow" : false});
        }
        {
            var Q0;
            Q0=makeQuery(id+"F20.opExtrude","CAP_FACE",FACE,{"disambiguationData":[OSD([sQuery(id+"F19.wireOp",EDGE,"E74"),sQuery(id+"F19.wireOp",EDGE,"E75"),sQuery(id+"F19.wireOp",EDGE,"E76"),sQuery(id+"F19.wireOp",EDGE,"E77"),sQuery(id+"F19.wireOp",EDGE,"E78"),sQuery(id+"F19.wireOp",EDGE,"E79"),sQuery(id+"F19.wireOp",EDGE,"E80")])],"isStart":true});
            var sketch = newSketch(context, id + "F54", { "sketchPlane" : qUnion([Q0])});
            skCircle(sketch, "E215", {"center": v(-2.55, 189.55) * mm, "radius": 3 * mm});
            skSolve(sketch);
        }
        {
            var Q0;
            Q0=makeQuery(id+"F54.imprint","IMPRINT",FACE,{"disambiguationData":[TD([[makeQuery(id+"F54.imprint","IMPRINT",EDGE,{"derivedFrom":sQuery(id+"F54.wireOp",EDGE,"E215")}),1.0]])]});
            extrude(context, id + "F55", {"entities" : qUnion([Q0]), "operationType" : NewBodyOperationType.REMOVE, "endBound" : BoundingType.THROUGH_ALL, "oppositeDirection" : true, "depth" : 25 * mm, "offsetDistance" : 25 * mm, "hasSecondDirection" : true, "secondDirectionBound" : SecondDirectionBoundingType.THROUGH_ALL, "secondDirectionOppositeDirection" : false, "secondDirectionDepth" : 25 * mm});
        }
        {
            var Q0;
            Q0=makeQuery(id+"F37.boolean.opBoolean","COPY",EDGE,{"derivedFrom":makeQuery(id+"F37.opExtrude","CAP_EDGE",EDGE,{"disambiguationData":[OSD([sQuery(id+"F36.wireOp",EDGE,"E176")])],"isStart":false})});
            fillet(context, id + "F56", {"entities" : qUnion([Q0]), "radius" : 2 * mm, "tangentPropagation" : true, "allowEdgeOverflow" : false});
        }
    });
